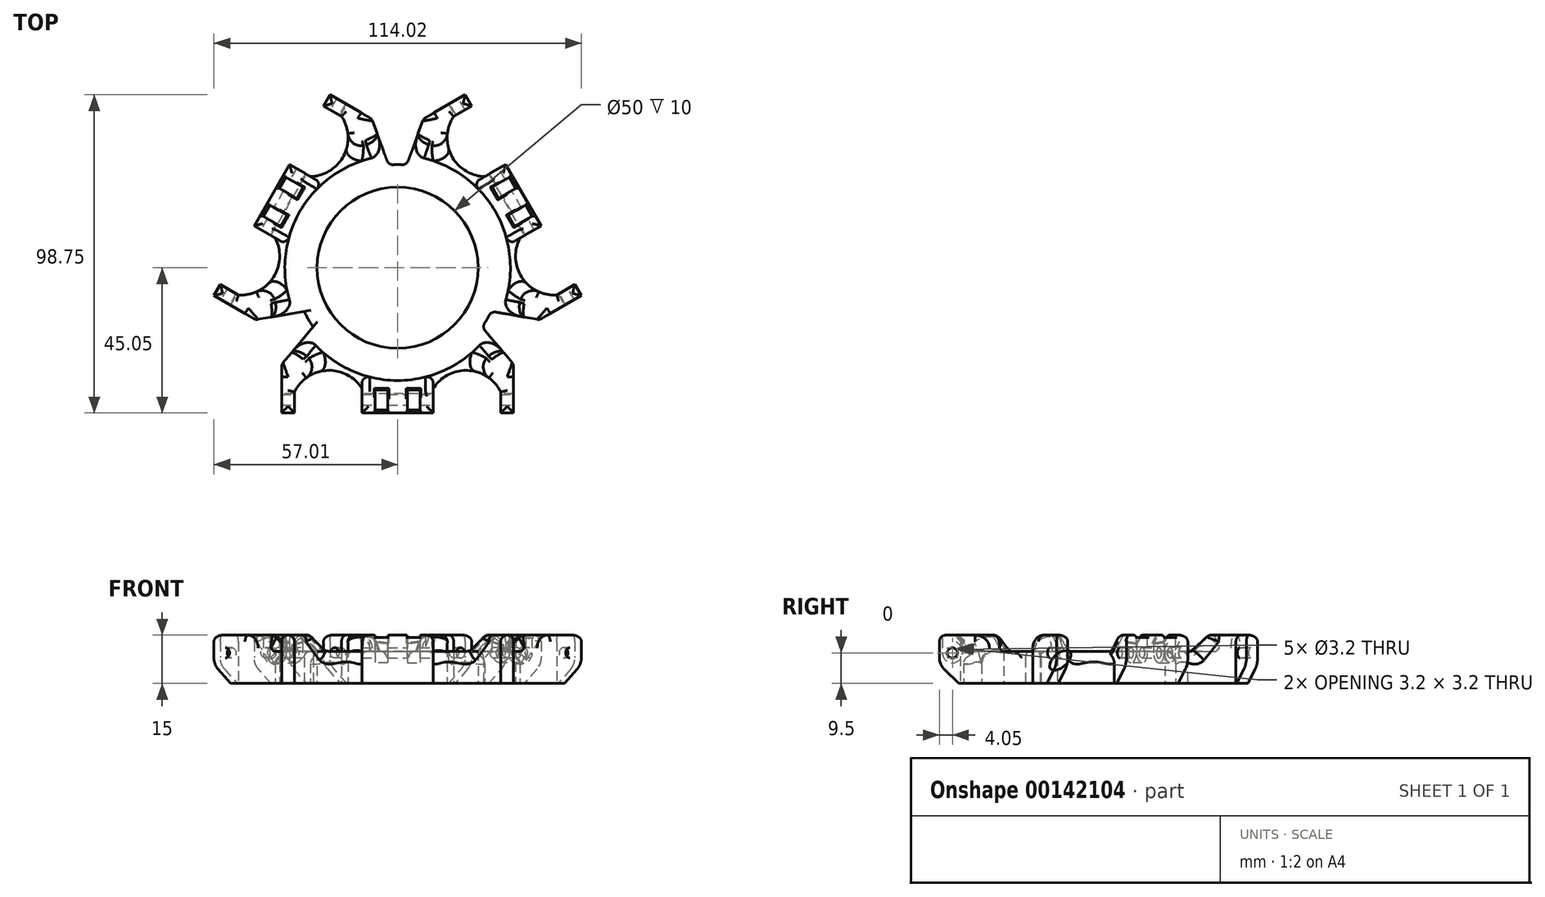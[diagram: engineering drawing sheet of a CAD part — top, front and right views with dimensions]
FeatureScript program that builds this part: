
annotation { "Feature Type Name" : "Feature", "Feature Type Description" : "" }
export const myFeature = defineFeature(function(context is Context, id is Id, definition is map)
    precondition{}
    {
        {
            assignVariable(context, id + "F0", {"name" : "JointHeight", "anyValue" : 18});
        }
        {
            var Q0;
            Q0=qCreatedBy(makeId("Top.planeOp"),FACE);
            var sketch = newSketch(context, id + "F1", { "sketchPlane" : qUnion([Q0])});
            skCircle(sketch, "E0", {"center": v(0, 0) * mm, "radius": 25 * mm});
            skCircle(sketch, "E1", {"center": v(0, 0) * mm, "radius": 32 * mm});
            skSolve(sketch);
        }
        {
            var Q0;
            Q0=qCreatedBy(makeId("Top.planeOp"),FACE);
            var sketch = newSketch(context, id + "F2", { "sketchPlane" : qUnion([Q0])});
            skLineSegment(sketch, "E2", {"start": v(-21.5, 50) * mm, "end": v(-21.5, -50) * mm, "construction": true});
            skLineSegment(sketch, "E3", {"start": v(21.5, 50) * mm, "end": v(21.5, -50) * mm, "construction": true});
            skLineSegment(sketch, "E4", {"start": v(-11, -50) * mm, "end": v(-11, -30.05) * mm, "construction": true});
            skLineSegment(sketch, "E5", {"start": v(11, -50) * mm, "end": v(11, -30.05) * mm, "construction": true});
            skLineSegment(sketch, "E6", {"start": v(-32, -50) * mm, "end": v(-32, 0) * mm, "construction": true});
            skLineSegment(sketch, "E7", {"start": v(32, -50) * mm, "end": v(32, 0) * mm, "construction": true});
            skLineSegment(sketch, "E8", {"start": v(0, -41.5) * mm, "end": v(0, -32) * mm, "construction": true});
            skLineSegment(sketch, "E9", {"start": v(-11, -30.05) * mm, "end": v(-11, -45.05) * mm});
            skLineSegment(sketch, "E10", {"start": v(-11, -45.05) * mm, "end": v(11, -45.05) * mm});
            skLineSegment(sketch, "E11", {"start": v(11, -45.05) * mm, "end": v(11, -30.05) * mm});
            skLineSegment(sketch, "E12", {"start": v(-32, -45.05) * mm, "end": v(-36, -45.05) * mm});
            skArc(sketch, "E13", {"start": v(-11, -30.05) * mm, "mid": v(0, -32) * mm, "end": v(11, -30.05) * mm});
            skLineSegment(sketch, "E14", {"start": v(-36, -45.05) * mm, "end": v(-36, -30.05) * mm});
            skLineSegment(sketch, "E15", {"start": v(-36, -30.05) * mm, "end": v(-26.2, -18.37) * mm});
            skCircle(sketch, "E16", {"center": v(-21.5, -41.5) * mm, "radius": 9.25 * mm, "construction": true});
            skLineSegment(sketch, "E17", {"start": v(-32, -45.05) * mm, "end": v(-32, -38.55) * mm});
            skArc(sketch, "E18", {"start": v(-11, -37.55) * mm, "mid": v(-21.8, -31.88) * mm, "end": v(-32, -38.55) * mm});
            skArc(sketch, "E19", {"start": v(-26.2, -18.37) * mm, "mid": v(-19.5, -25.38) * mm, "end": v(-11, -30.05) * mm});
            skLineSegment(sketch, "E20.MirrorCS", {"start": v(36, -45.05) * mm, "end": v(36, -30.05) * mm});
            skLineSegment(sketch, "E21.MirrorCS", {"start": v(32, -45.05) * mm, "end": v(36, -45.05) * mm});
            skLineSegment(sketch, "E22.MirrorCS", {"start": v(36, -30.05) * mm, "end": v(26.2, -18.37) * mm});
            skLineSegment(sketch, "E23.MirrorCS", {"start": v(32, -45.05) * mm, "end": v(32, -38.55) * mm});
            skArc(sketch, "E24.MirrorCS", {"start": v(11, -37.55) * mm, "mid": v(21.8, -31.88) * mm, "end": v(32, -38.55) * mm});
            skArc(sketch, "E25.MirrorCS", {"start": v(26.2, -18.37) * mm, "mid": v(19.5, -25.38) * mm, "end": v(11, -30.05) * mm});
            skSolve(sketch);
        }
        {
            var Q0;
            Q0=makeQuery(id+"F1.imprint","IMPRINT",FACE,{"disambiguationData":[TD([[makeQuery(id+"F1.imprint","IMPRINT",EDGE,{"derivedFrom":sQuery(id+"F1.wireOp",EDGE,"E0")}),-1.0]])]});
            extrude(context, id + "F3", {"entities" : qUnion([Q0]), "depth" : 10 * mm});
        }
        {
            var Q0;
            Q0=qSketchRegion(id+"F2",true);
            extrude(context, id + "F4", {"entities" : qUnion([Q0]), "depth" : (getVariable(context, 'JointHeight') - 3) * mm});
        }
        {
            var Q0;
            Q0=makeQuery(id+"F4.opExtrude","SWEPT_FACE",FACE,{"disambiguationData":[OSD([sQuery(id+"F2.wireOp",EDGE,"E20.MirrorCS")])]});
            var sketch = newSketch(context, id + "F5", { "sketchPlane" : qUnion([Q0])});
            skCircle(sketch, "E26", {"center": v(-41, 9.5) * mm, "radius": 1.6 * mm});
            skSolve(sketch);
        }
        {
            var Q0;
            Q0=makeQuery(id+"F5.imprint","IMPRINT",FACE,{"disambiguationData":[TD([[makeQuery(id+"F5.imprint","IMPRINT",EDGE,{"derivedFrom":sQuery(id+"F5.wireOp",EDGE,"E26")}),1.0]])]});
            var Q1;
            Q1=makeQuery(id+"F4.opExtrude","SWEPT_FACE",FACE,{"disambiguationData":[OSD([sQuery(id+"F2.wireOp",EDGE,"E14")])]});
            extrude(context, id + "F6", {"entities" : qUnion([Q0]), "operationType" : NewBodyOperationType.REMOVE, "endBound" : BoundingType.UP_TO_SURFACE, "oppositeDirection" : true, "endBoundEntityFace" : qUnion([Q1]), "depth" : 25 * mm});
        }
        {
            var Q0;
            Q0=makeQuery(id+"F4.opExtrude","SWEPT_BODY",BODY,{"disambiguationData":[OSD([sQuery(id+"F2.wireOp",EDGE,"E9"),sQuery(id+"F2.wireOp",EDGE,"E10"),sQuery(id+"F2.wireOp",EDGE,"E11"),sQuery(id+"F2.wireOp",EDGE,"E12"),sQuery(id+"F2.wireOp",EDGE,"E13"),sQuery(id+"F2.wireOp",EDGE,"E14"),sQuery(id+"F2.wireOp",EDGE,"E15"),sQuery(id+"F2.wireOp",EDGE,"E17"),sQuery(id+"F2.wireOp",EDGE,"E18"),sQuery(id+"F2.wireOp",EDGE,"E19"),sQuery(id+"F2.wireOp",EDGE,"E20.MirrorCS"),sQuery(id+"F2.wireOp",EDGE,"E21.MirrorCS"),sQuery(id+"F2.wireOp",EDGE,"E22.MirrorCS"),sQuery(id+"F2.wireOp",EDGE,"E23.MirrorCS"),sQuery(id+"F2.wireOp",EDGE,"E24.MirrorCS"),sQuery(id+"F2.wireOp",EDGE,"E25.MirrorCS")])]});
            var Q1;
            Q1=makeQuery(id+"F3.opExtrude","SWEPT_FACE",FACE,{"disambiguationData":[OSD([sQuery(id+"F1.wireOp",EDGE,"E1")])]});
            circularPattern(context, id + "F7", {"operationType" : NewBodyOperationType.ADD, "entities" : qUnion([Q0]), "axis" : qUnion([Q1]), "angle" : 120 * degree, "instanceCount" : 3});
        }
        {
            var Q0;
            Q0=makeQuery(id+"F4.opExtrude","CAP_EDGE",EDGE,{"disambiguationData":[OSD([sQuery(id+"F2.wireOp",EDGE,"E13"),sQuery(id+"F2.wireOp",EDGE,"E19"),sQuery(id+"F2.wireOp",EDGE,"E25.MirrorCS")])],"isStart":false});
            var Q1;
            Q1=makeQuery(id+"F7.opPattern","COPY",EDGE,{"derivedFrom":makeQuery(id+"F4.opExtrude","CAP_EDGE",EDGE,{"disambiguationData":[OSD([sQuery(id+"F2.wireOp",EDGE,"E13"),sQuery(id+"F2.wireOp",EDGE,"E19"),sQuery(id+"F2.wireOp",EDGE,"E25.MirrorCS")])],"isStart":false}),"instanceName":"1"});
            var Q2;
            Q2=makeQuery(id+"F7.opPattern","COPY",EDGE,{"derivedFrom":makeQuery(id+"F4.opExtrude","CAP_EDGE",EDGE,{"disambiguationData":[OSD([sQuery(id+"F2.wireOp",EDGE,"E13"),sQuery(id+"F2.wireOp",EDGE,"E19"),sQuery(id+"F2.wireOp",EDGE,"E25.MirrorCS")])],"isStart":false}),"instanceName":"2"});
            chamfer(context, id + "F8", {"entities" : qUnion([Q0, Q1, Q2]), "width" : 8 * mm});
        }
        {
            var Q0;
            Q0=makeQuery(id+"F8.opChamfer","BLEND_EDGE",EDGE,{"blendedFrom":[makeQuery(id+"F4.opExtrude","CAP_EDGE",EDGE,{"disambiguationData":[OSD([sQuery(id+"F2.wireOp",EDGE,"E13"),sQuery(id+"F2.wireOp",EDGE,"E19"),sQuery(id+"F2.wireOp",EDGE,"E25.MirrorCS")])],"isStart":false}),makeQuery(id+"F4.opExtrude","SWEPT_FACE",FACE,{"disambiguationData":[OSD([sQuery(id+"F2.wireOp",EDGE,"E24.MirrorCS")])]})],"blendedInto":[makeQuery(id+"F4.opExtrude","SWEPT_FACE",FACE,{"disambiguationData":[OSD([sQuery(id+"F2.wireOp",EDGE,"E24.MirrorCS")])]})]});
            var Q1;
            Q1=makeQuery(id+"F8.opChamfer","BLEND_EDGE",EDGE,{"blendedFrom":[makeQuery(id+"F4.opExtrude","CAP_EDGE",EDGE,{"disambiguationData":[OSD([sQuery(id+"F2.wireOp",EDGE,"E13"),sQuery(id+"F2.wireOp",EDGE,"E19"),sQuery(id+"F2.wireOp",EDGE,"E25.MirrorCS")])],"isStart":false}),makeQuery(id+"F4.opExtrude","SWEPT_FACE",FACE,{"disambiguationData":[OSD([sQuery(id+"F2.wireOp",EDGE,"E18")])]})],"blendedInto":[makeQuery(id+"F4.opExtrude","SWEPT_FACE",FACE,{"disambiguationData":[OSD([sQuery(id+"F2.wireOp",EDGE,"E18")])]})]});
            var Q2;
            Q2=makeQuery(id+"F8.opChamfer","BLEND_EDGE",EDGE,{"blendedFrom":[makeQuery(id+"F4.opExtrude","CAP_EDGE",EDGE,{"disambiguationData":[OSD([sQuery(id+"F2.wireOp",EDGE,"E13"),sQuery(id+"F2.wireOp",EDGE,"E19"),sQuery(id+"F2.wireOp",EDGE,"E25.MirrorCS")])],"isStart":false}),makeQuery(id+"F4.opExtrude","SWEPT_FACE",FACE,{"disambiguationData":[OSD([sQuery(id+"F2.wireOp",EDGE,"E22.MirrorCS")])]})],"blendedInto":[makeQuery(id+"F4.opExtrude","SWEPT_FACE",FACE,{"disambiguationData":[OSD([sQuery(id+"F2.wireOp",EDGE,"E22.MirrorCS")])]})]});
            var Q3;
            Q3=makeQuery(id+"F8.opChamfer","BLEND_EDGE",EDGE,{"blendedFrom":[makeQuery(id+"F4.opExtrude","CAP_EDGE",EDGE,{"disambiguationData":[OSD([sQuery(id+"F2.wireOp",EDGE,"E13"),sQuery(id+"F2.wireOp",EDGE,"E19"),sQuery(id+"F2.wireOp",EDGE,"E25.MirrorCS")])],"isStart":false}),makeQuery(id+"F4.opExtrude","SWEPT_FACE",FACE,{"disambiguationData":[OSD([sQuery(id+"F2.wireOp",EDGE,"E15")])]})],"blendedInto":[makeQuery(id+"F4.opExtrude","SWEPT_FACE",FACE,{"disambiguationData":[OSD([sQuery(id+"F2.wireOp",EDGE,"E15")])]})]});
            var Q4;
            Q4=makeQuery(id+"F8.opChamfer","BLEND_EDGE",EDGE,{"blendedFrom":[makeQuery(id+"F7.opPattern","COPY",EDGE,{"derivedFrom":makeQuery(id+"F4.opExtrude","CAP_EDGE",EDGE,{"disambiguationData":[OSD([sQuery(id+"F2.wireOp",EDGE,"E13"),sQuery(id+"F2.wireOp",EDGE,"E19"),sQuery(id+"F2.wireOp",EDGE,"E25.MirrorCS")])],"isStart":false}),"instanceName":"2"}),makeQuery(id+"F7.opPattern","COPY",FACE,{"derivedFrom":makeQuery(id+"F4.opExtrude","SWEPT_FACE",FACE,{"disambiguationData":[OSD([sQuery(id+"F2.wireOp",EDGE,"E18")])]}),"instanceName":"2"})],"blendedInto":[makeQuery(id+"F7.opPattern","COPY",FACE,{"derivedFrom":makeQuery(id+"F4.opExtrude","SWEPT_FACE",FACE,{"disambiguationData":[OSD([sQuery(id+"F2.wireOp",EDGE,"E18")])]}),"instanceName":"2"})]});
            var Q5;
            Q5=makeQuery(id+"F8.opChamfer","BLEND_EDGE",EDGE,{"blendedFrom":[makeQuery(id+"F7.opPattern","COPY",EDGE,{"derivedFrom":makeQuery(id+"F4.opExtrude","CAP_EDGE",EDGE,{"disambiguationData":[OSD([sQuery(id+"F2.wireOp",EDGE,"E13"),sQuery(id+"F2.wireOp",EDGE,"E19"),sQuery(id+"F2.wireOp",EDGE,"E25.MirrorCS")])],"isStart":false}),"instanceName":"1"}),makeQuery(id+"F7.opPattern","COPY",FACE,{"derivedFrom":makeQuery(id+"F4.opExtrude","SWEPT_FACE",FACE,{"disambiguationData":[OSD([sQuery(id+"F2.wireOp",EDGE,"E24.MirrorCS")])]}),"instanceName":"1"})],"blendedInto":[makeQuery(id+"F7.opPattern","COPY",FACE,{"derivedFrom":makeQuery(id+"F4.opExtrude","SWEPT_FACE",FACE,{"disambiguationData":[OSD([sQuery(id+"F2.wireOp",EDGE,"E24.MirrorCS")])]}),"instanceName":"1"})]});
            var Q6;
            Q6=makeQuery(id+"F8.opChamfer","BLEND_EDGE",EDGE,{"blendedFrom":[makeQuery(id+"F7.opPattern","COPY",EDGE,{"derivedFrom":makeQuery(id+"F4.opExtrude","CAP_EDGE",EDGE,{"disambiguationData":[OSD([sQuery(id+"F2.wireOp",EDGE,"E13"),sQuery(id+"F2.wireOp",EDGE,"E19"),sQuery(id+"F2.wireOp",EDGE,"E25.MirrorCS")])],"isStart":false}),"instanceName":"1"}),makeQuery(id+"F7.opPattern","COPY",FACE,{"derivedFrom":makeQuery(id+"F4.opExtrude","SWEPT_FACE",FACE,{"disambiguationData":[OSD([sQuery(id+"F2.wireOp",EDGE,"E18")])]}),"instanceName":"1"})],"blendedInto":[makeQuery(id+"F7.opPattern","COPY",FACE,{"derivedFrom":makeQuery(id+"F4.opExtrude","SWEPT_FACE",FACE,{"disambiguationData":[OSD([sQuery(id+"F2.wireOp",EDGE,"E18")])]}),"instanceName":"1"})]});
            var Q7;
            Q7=makeQuery(id+"F8.opChamfer","BLEND_EDGE",EDGE,{"blendedFrom":[makeQuery(id+"F7.opPattern","COPY",EDGE,{"derivedFrom":makeQuery(id+"F4.opExtrude","CAP_EDGE",EDGE,{"disambiguationData":[OSD([sQuery(id+"F2.wireOp",EDGE,"E13"),sQuery(id+"F2.wireOp",EDGE,"E19"),sQuery(id+"F2.wireOp",EDGE,"E25.MirrorCS")])],"isStart":false}),"instanceName":"2"}),makeQuery(id+"F7.opPattern","COPY",FACE,{"derivedFrom":makeQuery(id+"F4.opExtrude","SWEPT_FACE",FACE,{"disambiguationData":[OSD([sQuery(id+"F2.wireOp",EDGE,"E24.MirrorCS")])]}),"instanceName":"2"})],"blendedInto":[makeQuery(id+"F7.opPattern","COPY",FACE,{"derivedFrom":makeQuery(id+"F4.opExtrude","SWEPT_FACE",FACE,{"disambiguationData":[OSD([sQuery(id+"F2.wireOp",EDGE,"E24.MirrorCS")])]}),"instanceName":"2"})]});
            var Q8;
            Q8=makeQuery(id+"F8.opChamfer","BLEND_EDGE",EDGE,{"blendedFrom":[makeQuery(id+"F7.opPattern","COPY",EDGE,{"derivedFrom":makeQuery(id+"F4.opExtrude","CAP_EDGE",EDGE,{"disambiguationData":[OSD([sQuery(id+"F2.wireOp",EDGE,"E13"),sQuery(id+"F2.wireOp",EDGE,"E19"),sQuery(id+"F2.wireOp",EDGE,"E25.MirrorCS")])],"isStart":false}),"instanceName":"1"}),makeQuery(id+"F7.opPattern","COPY",FACE,{"derivedFrom":makeQuery(id+"F4.opExtrude","SWEPT_FACE",FACE,{"disambiguationData":[OSD([sQuery(id+"F2.wireOp",EDGE,"E22.MirrorCS")])]}),"instanceName":"1"})],"blendedInto":[makeQuery(id+"F7.opPattern","COPY",FACE,{"derivedFrom":makeQuery(id+"F4.opExtrude","SWEPT_FACE",FACE,{"disambiguationData":[OSD([sQuery(id+"F2.wireOp",EDGE,"E22.MirrorCS")])]}),"instanceName":"1"})]});
            var Q9;
            Q9=makeQuery(id+"F8.opChamfer","BLEND_EDGE",EDGE,{"blendedFrom":[makeQuery(id+"F7.opPattern","COPY",EDGE,{"derivedFrom":makeQuery(id+"F4.opExtrude","CAP_EDGE",EDGE,{"disambiguationData":[OSD([sQuery(id+"F2.wireOp",EDGE,"E13"),sQuery(id+"F2.wireOp",EDGE,"E19"),sQuery(id+"F2.wireOp",EDGE,"E25.MirrorCS")])],"isStart":false}),"instanceName":"1"}),makeQuery(id+"F7.opPattern","COPY",FACE,{"derivedFrom":makeQuery(id+"F4.opExtrude","SWEPT_FACE",FACE,{"disambiguationData":[OSD([sQuery(id+"F2.wireOp",EDGE,"E15")])]}),"instanceName":"1"})],"blendedInto":[makeQuery(id+"F7.opPattern","COPY",FACE,{"derivedFrom":makeQuery(id+"F4.opExtrude","SWEPT_FACE",FACE,{"disambiguationData":[OSD([sQuery(id+"F2.wireOp",EDGE,"E15")])]}),"instanceName":"1"})]});
            var Q10;
            Q10=makeQuery(id+"F8.opChamfer","BLEND_EDGE",EDGE,{"blendedFrom":[makeQuery(id+"F7.opPattern","COPY",EDGE,{"derivedFrom":makeQuery(id+"F4.opExtrude","CAP_EDGE",EDGE,{"disambiguationData":[OSD([sQuery(id+"F2.wireOp",EDGE,"E13"),sQuery(id+"F2.wireOp",EDGE,"E19"),sQuery(id+"F2.wireOp",EDGE,"E25.MirrorCS")])],"isStart":false}),"instanceName":"2"}),makeQuery(id+"F7.opPattern","COPY",FACE,{"derivedFrom":makeQuery(id+"F4.opExtrude","SWEPT_FACE",FACE,{"disambiguationData":[OSD([sQuery(id+"F2.wireOp",EDGE,"E22.MirrorCS")])]}),"instanceName":"2"})],"blendedInto":[makeQuery(id+"F7.opPattern","COPY",FACE,{"derivedFrom":makeQuery(id+"F4.opExtrude","SWEPT_FACE",FACE,{"disambiguationData":[OSD([sQuery(id+"F2.wireOp",EDGE,"E22.MirrorCS")])]}),"instanceName":"2"})]});
            var Q11;
            Q11=makeQuery(id+"F7.opPattern","COPY",EDGE,{"derivedFrom":makeQuery(id+"F4.opExtrude","CAP_EDGE",EDGE,{"disambiguationData":[OSD([sQuery(id+"F2.wireOp",EDGE,"E15")])],"isStart":false}),"instanceName":"2"});
            var Q12;
            Q12=makeQuery(id+"F4.opExtrude","CAP_EDGE",EDGE,{"disambiguationData":[OSD([sQuery(id+"F2.wireOp",EDGE,"E22.MirrorCS")])],"isStart":false});
            var Q13;
            Q13=makeQuery(id+"F8.opChamfer","BLEND_EDGE",EDGE,{"blendedFrom":[makeQuery(id+"F7.opPattern","COPY",EDGE,{"derivedFrom":makeQuery(id+"F4.opExtrude","CAP_EDGE",EDGE,{"disambiguationData":[OSD([sQuery(id+"F2.wireOp",EDGE,"E13"),sQuery(id+"F2.wireOp",EDGE,"E19"),sQuery(id+"F2.wireOp",EDGE,"E25.MirrorCS")])],"isStart":false}),"instanceName":"2"}),makeQuery(id+"F7.opPattern","COPY",FACE,{"derivedFrom":makeQuery(id+"F4.opExtrude","SWEPT_FACE",FACE,{"disambiguationData":[OSD([sQuery(id+"F2.wireOp",EDGE,"E15")])]}),"instanceName":"2"})],"blendedInto":[makeQuery(id+"F7.opPattern","COPY",FACE,{"derivedFrom":makeQuery(id+"F4.opExtrude","SWEPT_FACE",FACE,{"disambiguationData":[OSD([sQuery(id+"F2.wireOp",EDGE,"E15")])]}),"instanceName":"2"})]});
            var Q14;
            {var subQ0=sQuery(id+"F1.wireOp",EDGE,"E1");Q14=makeQuery(id+"F8.opChamfer","TWEAK_EDGE",EDGE,{"derivedFrom":[makeQuery(id+"F7.boolean.opBoolean","TWEAK_VERTEX",VERTEX,{"derivedFrom":[makeQuery(id+"F3.opExtrude","CAP_FACE",FACE,{"disambiguationData":[OSD([sQuery(id+"F1.wireOp",EDGE,"E0"),subQ0])],"isStart":false}),makeQuery(id+"F3.opExtrude","SWEPT_FACE",FACE,{"disambiguationData":[OSD([subQ0])]}),makeQuery(id+"F7.opPattern","COPY",FACE,{"derivedFrom":makeQuery(id+"F4.opExtrude","SWEPT_FACE",FACE,{"disambiguationData":[OSD([sQuery(id+"F2.wireOp",EDGE,"E13"),sQuery(id+"F2.wireOp",EDGE,"E19"),sQuery(id+"F2.wireOp",EDGE,"E25.MirrorCS")])]}),"instanceName":"2"}),makeQuery(id+"F7.opPattern","COPY",FACE,{"derivedFrom":makeQuery(id+"F4.opExtrude","SWEPT_FACE",FACE,{"disambiguationData":[OSD([sQuery(id+"F2.wireOp",EDGE,"E22.MirrorCS")])]}),"instanceName":"2"})]})]});}
            var Q15;
            {var subQ0=sQuery(id+"F1.wireOp",EDGE,"E1");Q15=makeQuery(id+"F8.opChamfer","TWEAK_EDGE",EDGE,{"derivedFrom":[makeQuery(id+"F7.boolean.opBoolean","TWEAK_VERTEX",VERTEX,{"derivedFrom":[makeQuery(id+"F3.opExtrude","CAP_FACE",FACE,{"disambiguationData":[OSD([sQuery(id+"F1.wireOp",EDGE,"E0"),subQ0])],"isStart":false}),makeQuery(id+"F3.opExtrude","SWEPT_FACE",FACE,{"disambiguationData":[OSD([subQ0])]}),makeQuery(id+"F7.opPattern","COPY",FACE,{"derivedFrom":makeQuery(id+"F4.opExtrude","SWEPT_FACE",FACE,{"disambiguationData":[OSD([sQuery(id+"F2.wireOp",EDGE,"E13"),sQuery(id+"F2.wireOp",EDGE,"E19"),sQuery(id+"F2.wireOp",EDGE,"E25.MirrorCS")])]}),"instanceName":"1"}),makeQuery(id+"F7.opPattern","COPY",FACE,{"derivedFrom":makeQuery(id+"F4.opExtrude","SWEPT_FACE",FACE,{"disambiguationData":[OSD([sQuery(id+"F2.wireOp",EDGE,"E15")])]}),"instanceName":"1"})]})]});}
            var Q16;
            {var subQ0=sQuery(id+"F1.wireOp",EDGE,"E1");Q16=makeQuery(id+"F8.opChamfer","TWEAK_EDGE",EDGE,{"derivedFrom":[makeQuery(id+"F7.boolean.opBoolean","TWEAK_VERTEX",VERTEX,{"derivedFrom":[makeQuery(id+"F3.opExtrude","CAP_FACE",FACE,{"disambiguationData":[OSD([sQuery(id+"F1.wireOp",EDGE,"E0"),subQ0])],"isStart":false}),makeQuery(id+"F3.opExtrude","SWEPT_FACE",FACE,{"disambiguationData":[OSD([subQ0])]}),makeQuery(id+"F7.opPattern","COPY",FACE,{"derivedFrom":makeQuery(id+"F4.opExtrude","SWEPT_FACE",FACE,{"disambiguationData":[OSD([sQuery(id+"F2.wireOp",EDGE,"E13"),sQuery(id+"F2.wireOp",EDGE,"E19"),sQuery(id+"F2.wireOp",EDGE,"E25.MirrorCS")])]}),"instanceName":"1"}),makeQuery(id+"F7.opPattern","COPY",FACE,{"derivedFrom":makeQuery(id+"F4.opExtrude","SWEPT_FACE",FACE,{"disambiguationData":[OSD([sQuery(id+"F2.wireOp",EDGE,"E22.MirrorCS")])]}),"instanceName":"1"})]})]});}
            var Q17;
            {var subQ0=sQuery(id+"F1.wireOp",EDGE,"E1");Q17=makeQuery(id+"F8.opChamfer","TWEAK_EDGE",EDGE,{"derivedFrom":[makeQuery(id+"F7.boolean.opBoolean","TWEAK_VERTEX",VERTEX,{"derivedFrom":[makeQuery(id+"F3.opExtrude","CAP_FACE",FACE,{"disambiguationData":[OSD([sQuery(id+"F1.wireOp",EDGE,"E0"),subQ0])],"isStart":false}),makeQuery(id+"F3.opExtrude","SWEPT_FACE",FACE,{"disambiguationData":[OSD([subQ0])]}),makeQuery(id+"F4.opExtrude","SWEPT_FACE",FACE,{"disambiguationData":[OSD([sQuery(id+"F2.wireOp",EDGE,"E13"),sQuery(id+"F2.wireOp",EDGE,"E19"),sQuery(id+"F2.wireOp",EDGE,"E25.MirrorCS")])]}),makeQuery(id+"F4.opExtrude","SWEPT_FACE",FACE,{"disambiguationData":[OSD([sQuery(id+"F2.wireOp",EDGE,"E15")])]})]})]});}
            var Q18;
            Q18=makeQuery(id+"F4.opExtrude","CAP_EDGE",EDGE,{"disambiguationData":[OSD([sQuery(id+"F2.wireOp",EDGE,"E15")])],"isStart":false});
            var Q19;
            Q19=makeQuery(id+"F7.opPattern","COPY",EDGE,{"derivedFrom":makeQuery(id+"F4.opExtrude","CAP_EDGE",EDGE,{"disambiguationData":[OSD([sQuery(id+"F2.wireOp",EDGE,"E22.MirrorCS")])],"isStart":false}),"instanceName":"1"});
            var Q20;
            Q20=makeQuery(id+"F7.opPattern","COPY",EDGE,{"derivedFrom":makeQuery(id+"F4.opExtrude","CAP_EDGE",EDGE,{"disambiguationData":[OSD([sQuery(id+"F2.wireOp",EDGE,"E22.MirrorCS")])],"isStart":false}),"instanceName":"2"});
            var Q21;
            Q21=makeQuery(id+"F7.opPattern","COPY",EDGE,{"derivedFrom":makeQuery(id+"F4.opExtrude","CAP_EDGE",EDGE,{"disambiguationData":[OSD([sQuery(id+"F2.wireOp",EDGE,"E15")])],"isStart":false}),"instanceName":"1"});
            var Q22;
            {var subQ0=sQuery(id+"F1.wireOp",EDGE,"E1");Q22=makeQuery(id+"F8.opChamfer","TWEAK_EDGE",EDGE,{"derivedFrom":[makeQuery(id+"F7.boolean.opBoolean","TWEAK_VERTEX",VERTEX,{"derivedFrom":[makeQuery(id+"F3.opExtrude","CAP_FACE",FACE,{"disambiguationData":[OSD([sQuery(id+"F1.wireOp",EDGE,"E0"),subQ0])],"isStart":false}),makeQuery(id+"F3.opExtrude","SWEPT_FACE",FACE,{"disambiguationData":[OSD([subQ0])]}),makeQuery(id+"F7.opPattern","COPY",FACE,{"derivedFrom":makeQuery(id+"F4.opExtrude","SWEPT_FACE",FACE,{"disambiguationData":[OSD([sQuery(id+"F2.wireOp",EDGE,"E13"),sQuery(id+"F2.wireOp",EDGE,"E19"),sQuery(id+"F2.wireOp",EDGE,"E25.MirrorCS")])]}),"instanceName":"2"}),makeQuery(id+"F7.opPattern","COPY",FACE,{"derivedFrom":makeQuery(id+"F4.opExtrude","SWEPT_FACE",FACE,{"disambiguationData":[OSD([sQuery(id+"F2.wireOp",EDGE,"E15")])]}),"instanceName":"2"})]})]});}
            var Q23;
            {var subQ0=sQuery(id+"F1.wireOp",EDGE,"E1");Q23=makeQuery(id+"F8.opChamfer","TWEAK_EDGE",EDGE,{"derivedFrom":[makeQuery(id+"F7.boolean.opBoolean","TWEAK_VERTEX",VERTEX,{"derivedFrom":[makeQuery(id+"F3.opExtrude","CAP_FACE",FACE,{"disambiguationData":[OSD([sQuery(id+"F1.wireOp",EDGE,"E0"),subQ0])],"isStart":false}),makeQuery(id+"F3.opExtrude","SWEPT_FACE",FACE,{"disambiguationData":[OSD([subQ0])]}),makeQuery(id+"F4.opExtrude","SWEPT_FACE",FACE,{"disambiguationData":[OSD([sQuery(id+"F2.wireOp",EDGE,"E13"),sQuery(id+"F2.wireOp",EDGE,"E19"),sQuery(id+"F2.wireOp",EDGE,"E25.MirrorCS")])]}),makeQuery(id+"F4.opExtrude","SWEPT_FACE",FACE,{"disambiguationData":[OSD([sQuery(id+"F2.wireOp",EDGE,"E22.MirrorCS")])]})]})]});}
            fillet(context, id + "F9", {"entities" : qUnion([Q0, Q1, Q2, Q3, Q4, Q5, Q6, Q7, Q8, Q9, Q10, Q11, Q12, Q13, Q14, Q15, Q16, Q17, Q18, Q19, Q20, Q21, Q22, Q23]), "radius" : 4 * mm, "tangentPropagation" : true, "allowEdgeOverflow" : false});
        }
        {
            var Q0;
            Q0=makeQuery(id+"F8.opChamfer","BLEND_EDGE",EDGE,{"blendedFrom":[makeQuery(id+"F7.opPattern","COPY",EDGE,{"derivedFrom":makeQuery(id+"F4.opExtrude","CAP_EDGE",EDGE,{"disambiguationData":[OSD([sQuery(id+"F2.wireOp",EDGE,"E13"),sQuery(id+"F2.wireOp",EDGE,"E19"),sQuery(id+"F2.wireOp",EDGE,"E25.MirrorCS")])],"isStart":false}),"instanceName":"1"}),makeQuery(id+"F7.opPattern","COPY",FACE,{"derivedFrom":makeQuery(id+"F4.opExtrude","SWEPT_FACE",FACE,{"disambiguationData":[OSD([sQuery(id+"F2.wireOp",EDGE,"E11")])]}),"instanceName":"1"})],"blendedInto":[makeQuery(id+"F7.opPattern","COPY",FACE,{"derivedFrom":makeQuery(id+"F4.opExtrude","SWEPT_FACE",FACE,{"disambiguationData":[OSD([sQuery(id+"F2.wireOp",EDGE,"E11")])]}),"instanceName":"1"})]});
            var Q1;
            Q1=makeQuery(id+"F8.opChamfer","BLEND_EDGE",EDGE,{"blendedFrom":[makeQuery(id+"F7.opPattern","COPY",EDGE,{"derivedFrom":makeQuery(id+"F4.opExtrude","CAP_EDGE",EDGE,{"disambiguationData":[OSD([sQuery(id+"F2.wireOp",EDGE,"E13"),sQuery(id+"F2.wireOp",EDGE,"E19"),sQuery(id+"F2.wireOp",EDGE,"E25.MirrorCS")])],"isStart":false}),"instanceName":"1"}),makeQuery(id+"F7.opPattern","COPY",FACE,{"derivedFrom":makeQuery(id+"F4.opExtrude","SWEPT_FACE",FACE,{"disambiguationData":[OSD([sQuery(id+"F2.wireOp",EDGE,"E9")])]}),"instanceName":"1"})],"blendedInto":[makeQuery(id+"F7.opPattern","COPY",FACE,{"derivedFrom":makeQuery(id+"F4.opExtrude","SWEPT_FACE",FACE,{"disambiguationData":[OSD([sQuery(id+"F2.wireOp",EDGE,"E9")])]}),"instanceName":"1"})]});
            var Q2;
            Q2=makeQuery(id+"F8.opChamfer","BLEND_EDGE",EDGE,{"blendedFrom":[makeQuery(id+"F7.opPattern","COPY",EDGE,{"derivedFrom":makeQuery(id+"F4.opExtrude","CAP_EDGE",EDGE,{"disambiguationData":[OSD([sQuery(id+"F2.wireOp",EDGE,"E13"),sQuery(id+"F2.wireOp",EDGE,"E19"),sQuery(id+"F2.wireOp",EDGE,"E25.MirrorCS")])],"isStart":false}),"instanceName":"2"}),makeQuery(id+"F7.opPattern","COPY",FACE,{"derivedFrom":makeQuery(id+"F4.opExtrude","SWEPT_FACE",FACE,{"disambiguationData":[OSD([sQuery(id+"F2.wireOp",EDGE,"E11")])]}),"instanceName":"2"})],"blendedInto":[makeQuery(id+"F7.opPattern","COPY",FACE,{"derivedFrom":makeQuery(id+"F4.opExtrude","SWEPT_FACE",FACE,{"disambiguationData":[OSD([sQuery(id+"F2.wireOp",EDGE,"E11")])]}),"instanceName":"2"})]});
            var Q3;
            Q3=makeQuery(id+"F8.opChamfer","BLEND_EDGE",EDGE,{"blendedFrom":[makeQuery(id+"F7.opPattern","COPY",EDGE,{"derivedFrom":makeQuery(id+"F4.opExtrude","CAP_EDGE",EDGE,{"disambiguationData":[OSD([sQuery(id+"F2.wireOp",EDGE,"E13"),sQuery(id+"F2.wireOp",EDGE,"E19"),sQuery(id+"F2.wireOp",EDGE,"E25.MirrorCS")])],"isStart":false}),"instanceName":"2"}),makeQuery(id+"F7.opPattern","COPY",FACE,{"derivedFrom":makeQuery(id+"F4.opExtrude","SWEPT_FACE",FACE,{"disambiguationData":[OSD([sQuery(id+"F2.wireOp",EDGE,"E9")])]}),"instanceName":"2"})],"blendedInto":[makeQuery(id+"F7.opPattern","COPY",FACE,{"derivedFrom":makeQuery(id+"F4.opExtrude","SWEPT_FACE",FACE,{"disambiguationData":[OSD([sQuery(id+"F2.wireOp",EDGE,"E9")])]}),"instanceName":"2"})]});
            var Q4;
            Q4=makeQuery(id+"F8.opChamfer","BLEND_EDGE",EDGE,{"blendedFrom":[makeQuery(id+"F4.opExtrude","CAP_EDGE",EDGE,{"disambiguationData":[OSD([sQuery(id+"F2.wireOp",EDGE,"E13"),sQuery(id+"F2.wireOp",EDGE,"E19"),sQuery(id+"F2.wireOp",EDGE,"E25.MirrorCS")])],"isStart":false}),makeQuery(id+"F4.opExtrude","SWEPT_FACE",FACE,{"disambiguationData":[OSD([sQuery(id+"F2.wireOp",EDGE,"E11")])]})],"blendedInto":[makeQuery(id+"F4.opExtrude","SWEPT_FACE",FACE,{"disambiguationData":[OSD([sQuery(id+"F2.wireOp",EDGE,"E11")])]})]});
            var Q5;
            Q5=makeQuery(id+"F8.opChamfer","BLEND_EDGE",EDGE,{"blendedFrom":[makeQuery(id+"F4.opExtrude","CAP_EDGE",EDGE,{"disambiguationData":[OSD([sQuery(id+"F2.wireOp",EDGE,"E13"),sQuery(id+"F2.wireOp",EDGE,"E19"),sQuery(id+"F2.wireOp",EDGE,"E25.MirrorCS")])],"isStart":false}),makeQuery(id+"F4.opExtrude","SWEPT_FACE",FACE,{"disambiguationData":[OSD([sQuery(id+"F2.wireOp",EDGE,"E9")])]})],"blendedInto":[makeQuery(id+"F4.opExtrude","SWEPT_FACE",FACE,{"disambiguationData":[OSD([sQuery(id+"F2.wireOp",EDGE,"E9")])]})]});
            var Q6;
            Q6=makeQuery(id+"F8.opChamfer","SPLIT",FACE,{"disambiguationData":[OD(0.0)],"derivedFrom":makeQuery(id+"F4.opExtrude","CAP_FACE",FACE,{"disambiguationData":[OSD([sQuery(id+"F2.wireOp",EDGE,"E9"),sQuery(id+"F2.wireOp",EDGE,"E10"),sQuery(id+"F2.wireOp",EDGE,"E11"),sQuery(id+"F2.wireOp",EDGE,"E12"),sQuery(id+"F2.wireOp",EDGE,"E13"),sQuery(id+"F2.wireOp",EDGE,"E14"),sQuery(id+"F2.wireOp",EDGE,"E15"),sQuery(id+"F2.wireOp",EDGE,"E17"),sQuery(id+"F2.wireOp",EDGE,"E18"),sQuery(id+"F2.wireOp",EDGE,"E19"),sQuery(id+"F2.wireOp",EDGE,"E20.MirrorCS"),sQuery(id+"F2.wireOp",EDGE,"E21.MirrorCS"),sQuery(id+"F2.wireOp",EDGE,"E22.MirrorCS"),sQuery(id+"F2.wireOp",EDGE,"E23.MirrorCS"),sQuery(id+"F2.wireOp",EDGE,"E24.MirrorCS"),sQuery(id+"F2.wireOp",EDGE,"E25.MirrorCS")])],"isStart":false})});
            var Q7;
            Q7=makeQuery(id+"F8.opChamfer","SPLIT",FACE,{"disambiguationData":[OD(1.0)],"derivedFrom":makeQuery(id+"F4.opExtrude","CAP_FACE",FACE,{"disambiguationData":[OSD([sQuery(id+"F2.wireOp",EDGE,"E9"),sQuery(id+"F2.wireOp",EDGE,"E10"),sQuery(id+"F2.wireOp",EDGE,"E11"),sQuery(id+"F2.wireOp",EDGE,"E12"),sQuery(id+"F2.wireOp",EDGE,"E13"),sQuery(id+"F2.wireOp",EDGE,"E14"),sQuery(id+"F2.wireOp",EDGE,"E15"),sQuery(id+"F2.wireOp",EDGE,"E17"),sQuery(id+"F2.wireOp",EDGE,"E18"),sQuery(id+"F2.wireOp",EDGE,"E19"),sQuery(id+"F2.wireOp",EDGE,"E20.MirrorCS"),sQuery(id+"F2.wireOp",EDGE,"E21.MirrorCS"),sQuery(id+"F2.wireOp",EDGE,"E22.MirrorCS"),sQuery(id+"F2.wireOp",EDGE,"E23.MirrorCS"),sQuery(id+"F2.wireOp",EDGE,"E24.MirrorCS"),sQuery(id+"F2.wireOp",EDGE,"E25.MirrorCS")])],"isStart":false})});
            var Q8;
            Q8=makeQuery(id+"F8.opChamfer","SPLIT",FACE,{"disambiguationData":[OD(2.0)],"derivedFrom":makeQuery(id+"F7.opPattern","COPY",FACE,{"derivedFrom":makeQuery(id+"F4.opExtrude","CAP_FACE",FACE,{"disambiguationData":[OSD([sQuery(id+"F2.wireOp",EDGE,"E9"),sQuery(id+"F2.wireOp",EDGE,"E10"),sQuery(id+"F2.wireOp",EDGE,"E11"),sQuery(id+"F2.wireOp",EDGE,"E12"),sQuery(id+"F2.wireOp",EDGE,"E13"),sQuery(id+"F2.wireOp",EDGE,"E14"),sQuery(id+"F2.wireOp",EDGE,"E15"),sQuery(id+"F2.wireOp",EDGE,"E17"),sQuery(id+"F2.wireOp",EDGE,"E18"),sQuery(id+"F2.wireOp",EDGE,"E19"),sQuery(id+"F2.wireOp",EDGE,"E20.MirrorCS"),sQuery(id+"F2.wireOp",EDGE,"E21.MirrorCS"),sQuery(id+"F2.wireOp",EDGE,"E22.MirrorCS"),sQuery(id+"F2.wireOp",EDGE,"E23.MirrorCS"),sQuery(id+"F2.wireOp",EDGE,"E24.MirrorCS"),sQuery(id+"F2.wireOp",EDGE,"E25.MirrorCS")])],"isStart":false}),"instanceName":"1"})});
            var Q9;
            Q9=makeQuery(id+"F8.opChamfer","SPLIT",FACE,{"disambiguationData":[OD(1.0)],"derivedFrom":makeQuery(id+"F7.opPattern","COPY",FACE,{"derivedFrom":makeQuery(id+"F4.opExtrude","CAP_FACE",FACE,{"disambiguationData":[OSD([sQuery(id+"F2.wireOp",EDGE,"E9"),sQuery(id+"F2.wireOp",EDGE,"E10"),sQuery(id+"F2.wireOp",EDGE,"E11"),sQuery(id+"F2.wireOp",EDGE,"E12"),sQuery(id+"F2.wireOp",EDGE,"E13"),sQuery(id+"F2.wireOp",EDGE,"E14"),sQuery(id+"F2.wireOp",EDGE,"E15"),sQuery(id+"F2.wireOp",EDGE,"E17"),sQuery(id+"F2.wireOp",EDGE,"E18"),sQuery(id+"F2.wireOp",EDGE,"E19"),sQuery(id+"F2.wireOp",EDGE,"E20.MirrorCS"),sQuery(id+"F2.wireOp",EDGE,"E21.MirrorCS"),sQuery(id+"F2.wireOp",EDGE,"E22.MirrorCS"),sQuery(id+"F2.wireOp",EDGE,"E23.MirrorCS"),sQuery(id+"F2.wireOp",EDGE,"E24.MirrorCS"),sQuery(id+"F2.wireOp",EDGE,"E25.MirrorCS")])],"isStart":false}),"instanceName":"1"})});
            var Q10;
            Q10=makeQuery(id+"F8.opChamfer","SPLIT",FACE,{"disambiguationData":[OD(0.0)],"derivedFrom":makeQuery(id+"F7.opPattern","COPY",FACE,{"derivedFrom":makeQuery(id+"F4.opExtrude","CAP_FACE",FACE,{"disambiguationData":[OSD([sQuery(id+"F2.wireOp",EDGE,"E9"),sQuery(id+"F2.wireOp",EDGE,"E10"),sQuery(id+"F2.wireOp",EDGE,"E11"),sQuery(id+"F2.wireOp",EDGE,"E12"),sQuery(id+"F2.wireOp",EDGE,"E13"),sQuery(id+"F2.wireOp",EDGE,"E14"),sQuery(id+"F2.wireOp",EDGE,"E15"),sQuery(id+"F2.wireOp",EDGE,"E17"),sQuery(id+"F2.wireOp",EDGE,"E18"),sQuery(id+"F2.wireOp",EDGE,"E19"),sQuery(id+"F2.wireOp",EDGE,"E20.MirrorCS"),sQuery(id+"F2.wireOp",EDGE,"E21.MirrorCS"),sQuery(id+"F2.wireOp",EDGE,"E22.MirrorCS"),sQuery(id+"F2.wireOp",EDGE,"E23.MirrorCS"),sQuery(id+"F2.wireOp",EDGE,"E24.MirrorCS"),sQuery(id+"F2.wireOp",EDGE,"E25.MirrorCS")])],"isStart":false}),"instanceName":"1"})});
            var Q11;
            Q11=makeQuery(id+"F8.opChamfer","SPLIT",FACE,{"disambiguationData":[OD(2.0)],"derivedFrom":makeQuery(id+"F7.opPattern","COPY",FACE,{"derivedFrom":makeQuery(id+"F4.opExtrude","CAP_FACE",FACE,{"disambiguationData":[OSD([sQuery(id+"F2.wireOp",EDGE,"E9"),sQuery(id+"F2.wireOp",EDGE,"E10"),sQuery(id+"F2.wireOp",EDGE,"E11"),sQuery(id+"F2.wireOp",EDGE,"E12"),sQuery(id+"F2.wireOp",EDGE,"E13"),sQuery(id+"F2.wireOp",EDGE,"E14"),sQuery(id+"F2.wireOp",EDGE,"E15"),sQuery(id+"F2.wireOp",EDGE,"E17"),sQuery(id+"F2.wireOp",EDGE,"E18"),sQuery(id+"F2.wireOp",EDGE,"E19"),sQuery(id+"F2.wireOp",EDGE,"E20.MirrorCS"),sQuery(id+"F2.wireOp",EDGE,"E21.MirrorCS"),sQuery(id+"F2.wireOp",EDGE,"E22.MirrorCS"),sQuery(id+"F2.wireOp",EDGE,"E23.MirrorCS"),sQuery(id+"F2.wireOp",EDGE,"E24.MirrorCS"),sQuery(id+"F2.wireOp",EDGE,"E25.MirrorCS")])],"isStart":false}),"instanceName":"2"})});
            var Q12;
            Q12=makeQuery(id+"F8.opChamfer","SPLIT",FACE,{"disambiguationData":[OD(0.0)],"derivedFrom":makeQuery(id+"F7.opPattern","COPY",FACE,{"derivedFrom":makeQuery(id+"F4.opExtrude","CAP_FACE",FACE,{"disambiguationData":[OSD([sQuery(id+"F2.wireOp",EDGE,"E9"),sQuery(id+"F2.wireOp",EDGE,"E10"),sQuery(id+"F2.wireOp",EDGE,"E11"),sQuery(id+"F2.wireOp",EDGE,"E12"),sQuery(id+"F2.wireOp",EDGE,"E13"),sQuery(id+"F2.wireOp",EDGE,"E14"),sQuery(id+"F2.wireOp",EDGE,"E15"),sQuery(id+"F2.wireOp",EDGE,"E17"),sQuery(id+"F2.wireOp",EDGE,"E18"),sQuery(id+"F2.wireOp",EDGE,"E19"),sQuery(id+"F2.wireOp",EDGE,"E20.MirrorCS"),sQuery(id+"F2.wireOp",EDGE,"E21.MirrorCS"),sQuery(id+"F2.wireOp",EDGE,"E22.MirrorCS"),sQuery(id+"F2.wireOp",EDGE,"E23.MirrorCS"),sQuery(id+"F2.wireOp",EDGE,"E24.MirrorCS"),sQuery(id+"F2.wireOp",EDGE,"E25.MirrorCS")])],"isStart":false}),"instanceName":"2"})});
            var Q13;
            Q13=makeQuery(id+"F8.opChamfer","SPLIT",FACE,{"disambiguationData":[OD(1.0)],"derivedFrom":makeQuery(id+"F7.opPattern","COPY",FACE,{"derivedFrom":makeQuery(id+"F4.opExtrude","CAP_FACE",FACE,{"disambiguationData":[OSD([sQuery(id+"F2.wireOp",EDGE,"E9"),sQuery(id+"F2.wireOp",EDGE,"E10"),sQuery(id+"F2.wireOp",EDGE,"E11"),sQuery(id+"F2.wireOp",EDGE,"E12"),sQuery(id+"F2.wireOp",EDGE,"E13"),sQuery(id+"F2.wireOp",EDGE,"E14"),sQuery(id+"F2.wireOp",EDGE,"E15"),sQuery(id+"F2.wireOp",EDGE,"E17"),sQuery(id+"F2.wireOp",EDGE,"E18"),sQuery(id+"F2.wireOp",EDGE,"E19"),sQuery(id+"F2.wireOp",EDGE,"E20.MirrorCS"),sQuery(id+"F2.wireOp",EDGE,"E21.MirrorCS"),sQuery(id+"F2.wireOp",EDGE,"E22.MirrorCS"),sQuery(id+"F2.wireOp",EDGE,"E23.MirrorCS"),sQuery(id+"F2.wireOp",EDGE,"E24.MirrorCS"),sQuery(id+"F2.wireOp",EDGE,"E25.MirrorCS")])],"isStart":false}),"instanceName":"2"})});
            var Q14;
            Q14=makeQuery(id+"F8.opChamfer","SPLIT",FACE,{"disambiguationData":[OD(2.0)],"derivedFrom":makeQuery(id+"F4.opExtrude","CAP_FACE",FACE,{"disambiguationData":[OSD([sQuery(id+"F2.wireOp",EDGE,"E9"),sQuery(id+"F2.wireOp",EDGE,"E10"),sQuery(id+"F2.wireOp",EDGE,"E11"),sQuery(id+"F2.wireOp",EDGE,"E12"),sQuery(id+"F2.wireOp",EDGE,"E13"),sQuery(id+"F2.wireOp",EDGE,"E14"),sQuery(id+"F2.wireOp",EDGE,"E15"),sQuery(id+"F2.wireOp",EDGE,"E17"),sQuery(id+"F2.wireOp",EDGE,"E18"),sQuery(id+"F2.wireOp",EDGE,"E19"),sQuery(id+"F2.wireOp",EDGE,"E20.MirrorCS"),sQuery(id+"F2.wireOp",EDGE,"E21.MirrorCS"),sQuery(id+"F2.wireOp",EDGE,"E22.MirrorCS"),sQuery(id+"F2.wireOp",EDGE,"E23.MirrorCS"),sQuery(id+"F2.wireOp",EDGE,"E24.MirrorCS"),sQuery(id+"F2.wireOp",EDGE,"E25.MirrorCS")])],"isStart":false})});
            fillet(context, id + "F10", {"entities" : qUnion([Q0, Q1, Q2, Q3, Q4, Q5, Q6, Q7, Q8, Q9, Q10, Q11, Q12, Q13, Q14]), "radius" : 2 * mm, "tangentPropagation" : true, "allowEdgeOverflow" : false});
        }
        {
            var Q0;
            {var subQ0=sQuery(id+"F1.wireOp",EDGE,"E1");Q0=makeQuery(id+"F8.opChamfer","TWEAK_EDGE",EDGE,{"derivedFrom":[makeQuery(id+"F7.boolean.opBoolean","TWEAK_VERTEX",VERTEX,{"derivedFrom":[makeQuery(id+"F3.opExtrude","CAP_FACE",FACE,{"disambiguationData":[OSD([sQuery(id+"F1.wireOp",EDGE,"E0"),subQ0])],"isStart":false}),makeQuery(id+"F3.opExtrude","SWEPT_FACE",FACE,{"disambiguationData":[OSD([subQ0])]}),makeQuery(id+"F4.opExtrude","SWEPT_FACE",FACE,{"disambiguationData":[OSD([sQuery(id+"F2.wireOp",EDGE,"E13"),sQuery(id+"F2.wireOp",EDGE,"E19"),sQuery(id+"F2.wireOp",EDGE,"E25.MirrorCS")])]}),makeQuery(id+"F4.opExtrude","SWEPT_FACE",FACE,{"disambiguationData":[OSD([sQuery(id+"F2.wireOp",EDGE,"E15")])]})]})]});}
            var Q1;
            {var subQ0=makeQuery(id+"F4.opExtrude","SWEPT_FACE",FACE,{"disambiguationData":[OSD([sQuery(id+"F2.wireOp",EDGE,"E13"),sQuery(id+"F2.wireOp",EDGE,"E19"),sQuery(id+"F2.wireOp",EDGE,"E25.MirrorCS")])]});var subQ1=sQuery(id+"F1.wireOp",EDGE,"E1");Q1=makeQuery(id+"F7.boolean.opBoolean","SPLIT",EDGE,{"disambiguationData":[TD([makeQuery(id+"F3.opExtrude","CAP_FACE",FACE,{"disambiguationData":[OSD([sQuery(id+"F1.wireOp",EDGE,"E0"),subQ1])],"isStart":false}),makeQuery(id+"F3.opExtrude","SWEPT_FACE",FACE,{"disambiguationData":[OSD([subQ1])]}),subQ0,makeQuery(id+"F4.opExtrude","SWEPT_FACE",FACE,{"disambiguationData":[OSD([sQuery(id+"F2.wireOp",EDGE,"E15")])]}),makeQuery(id+"F7.opPattern","COPY",FACE,{"derivedFrom":subQ0,"instanceName":"1"}),makeQuery(id+"F7.opPattern","COPY",FACE,{"derivedFrom":makeQuery(id+"F4.opExtrude","SWEPT_FACE",FACE,{"disambiguationData":[OSD([sQuery(id+"F2.wireOp",EDGE,"E22.MirrorCS")])]}),"instanceName":"1"})])],"derivedFrom":makeQuery(id+"F3.opExtrude","CAP_EDGE",EDGE,{"disambiguationData":[OSD([subQ1])],"isStart":false})});}
            var Q2;
            {var subQ0=sQuery(id+"F1.wireOp",EDGE,"E1");Q2=makeQuery(id+"F8.opChamfer","TWEAK_EDGE",EDGE,{"derivedFrom":[makeQuery(id+"F7.boolean.opBoolean","TWEAK_VERTEX",VERTEX,{"derivedFrom":[makeQuery(id+"F3.opExtrude","CAP_FACE",FACE,{"disambiguationData":[OSD([sQuery(id+"F1.wireOp",EDGE,"E0"),subQ0])],"isStart":false}),makeQuery(id+"F3.opExtrude","SWEPT_FACE",FACE,{"disambiguationData":[OSD([subQ0])]}),makeQuery(id+"F7.opPattern","COPY",FACE,{"derivedFrom":makeQuery(id+"F4.opExtrude","SWEPT_FACE",FACE,{"disambiguationData":[OSD([sQuery(id+"F2.wireOp",EDGE,"E13"),sQuery(id+"F2.wireOp",EDGE,"E19"),sQuery(id+"F2.wireOp",EDGE,"E25.MirrorCS")])]}),"instanceName":"1"}),makeQuery(id+"F7.opPattern","COPY",FACE,{"derivedFrom":makeQuery(id+"F4.opExtrude","SWEPT_FACE",FACE,{"disambiguationData":[OSD([sQuery(id+"F2.wireOp",EDGE,"E22.MirrorCS")])]}),"instanceName":"1"})]})]});}
            var Q3;
            {var subQ0=sQuery(id+"F1.wireOp",EDGE,"E1");var subQ1=sQuery(id+"F1.wireOp",EDGE,"E0");var subQ3=sQuery(id+"F2.wireOp",EDGE,"E19");var subQ5=sQuery(id+"F2.wireOp",EDGE,"E15");Q3=makeQuery(id+"F7.boolean.opBoolean","SPLIT",EDGE,{"disambiguationData":[TD([makeQuery(id+"F3.opExtrude","CAP_FACE",FACE,{"disambiguationData":[OSD([subQ1,subQ0])],"isStart":true})])],"derivedFrom":makeQuery(id+"F4.opExtrude","SWEPT_EDGE",EDGE,{"disambiguationData":[OSD([subQ5,subQ3])]})});}
            var Q4;
            {var subQ0=sQuery(id+"F1.wireOp",EDGE,"E1");var subQ1=sQuery(id+"F1.wireOp",EDGE,"E0");var subQ2=sQuery(id+"F2.wireOp",EDGE,"E25.MirrorCS");var subQ3=sQuery(id+"F2.wireOp",EDGE,"E22.MirrorCS");Q4=makeQuery(id+"F7.boolean.opBoolean","SPLIT",EDGE,{"disambiguationData":[TD([makeQuery(id+"F3.opExtrude","CAP_FACE",FACE,{"disambiguationData":[OSD([subQ1,subQ0])],"isStart":true})])],"derivedFrom":makeQuery(id+"F7.opPattern","COPY",EDGE,{"derivedFrom":makeQuery(id+"F4.opExtrude","SWEPT_EDGE",EDGE,{"disambiguationData":[OSD([subQ3,subQ2])]}),"instanceName":"1"})});}
            var Q5;
            {var subQ0=sQuery(id+"F1.wireOp",EDGE,"E1");Q5=makeQuery(id+"F8.opChamfer","TWEAK_EDGE",EDGE,{"derivedFrom":[makeQuery(id+"F7.boolean.opBoolean","TWEAK_VERTEX",VERTEX,{"derivedFrom":[makeQuery(id+"F3.opExtrude","CAP_FACE",FACE,{"disambiguationData":[OSD([sQuery(id+"F1.wireOp",EDGE,"E0"),subQ0])],"isStart":false}),makeQuery(id+"F3.opExtrude","SWEPT_FACE",FACE,{"disambiguationData":[OSD([subQ0])]}),makeQuery(id+"F7.opPattern","COPY",FACE,{"derivedFrom":makeQuery(id+"F4.opExtrude","SWEPT_FACE",FACE,{"disambiguationData":[OSD([sQuery(id+"F2.wireOp",EDGE,"E13"),sQuery(id+"F2.wireOp",EDGE,"E19"),sQuery(id+"F2.wireOp",EDGE,"E25.MirrorCS")])]}),"instanceName":"1"}),makeQuery(id+"F7.opPattern","COPY",FACE,{"derivedFrom":makeQuery(id+"F4.opExtrude","SWEPT_FACE",FACE,{"disambiguationData":[OSD([sQuery(id+"F2.wireOp",EDGE,"E15")])]}),"instanceName":"1"})]})]});}
            var Q6;
            {var subQ0=makeQuery(id+"F4.opExtrude","SWEPT_FACE",FACE,{"disambiguationData":[OSD([sQuery(id+"F2.wireOp",EDGE,"E13"),sQuery(id+"F2.wireOp",EDGE,"E19"),sQuery(id+"F2.wireOp",EDGE,"E25.MirrorCS")])]});var subQ1=sQuery(id+"F1.wireOp",EDGE,"E1");Q6=makeQuery(id+"F7.boolean.opBoolean","SPLIT",EDGE,{"disambiguationData":[TD([makeQuery(id+"F3.opExtrude","CAP_FACE",FACE,{"disambiguationData":[OSD([sQuery(id+"F1.wireOp",EDGE,"E0"),subQ1])],"isStart":false}),makeQuery(id+"F3.opExtrude","SWEPT_FACE",FACE,{"disambiguationData":[OSD([subQ1])]}),makeQuery(id+"F7.opPattern","COPY",FACE,{"derivedFrom":subQ0,"instanceName":"1"}),makeQuery(id+"F7.opPattern","COPY",FACE,{"derivedFrom":makeQuery(id+"F4.opExtrude","SWEPT_FACE",FACE,{"disambiguationData":[OSD([sQuery(id+"F2.wireOp",EDGE,"E15")])]}),"instanceName":"1"}),makeQuery(id+"F7.opPattern","COPY",FACE,{"derivedFrom":subQ0,"instanceName":"2"}),makeQuery(id+"F7.opPattern","COPY",FACE,{"derivedFrom":makeQuery(id+"F4.opExtrude","SWEPT_FACE",FACE,{"disambiguationData":[OSD([sQuery(id+"F2.wireOp",EDGE,"E22.MirrorCS")])]}),"instanceName":"2"})])],"derivedFrom":makeQuery(id+"F3.opExtrude","CAP_EDGE",EDGE,{"disambiguationData":[OSD([subQ1])],"isStart":false})});}
            var Q7;
            {var subQ0=sQuery(id+"F1.wireOp",EDGE,"E1");Q7=makeQuery(id+"F8.opChamfer","TWEAK_EDGE",EDGE,{"derivedFrom":[makeQuery(id+"F7.boolean.opBoolean","TWEAK_VERTEX",VERTEX,{"derivedFrom":[makeQuery(id+"F3.opExtrude","CAP_FACE",FACE,{"disambiguationData":[OSD([sQuery(id+"F1.wireOp",EDGE,"E0"),subQ0])],"isStart":false}),makeQuery(id+"F3.opExtrude","SWEPT_FACE",FACE,{"disambiguationData":[OSD([subQ0])]}),makeQuery(id+"F7.opPattern","COPY",FACE,{"derivedFrom":makeQuery(id+"F4.opExtrude","SWEPT_FACE",FACE,{"disambiguationData":[OSD([sQuery(id+"F2.wireOp",EDGE,"E13"),sQuery(id+"F2.wireOp",EDGE,"E19"),sQuery(id+"F2.wireOp",EDGE,"E25.MirrorCS")])]}),"instanceName":"2"}),makeQuery(id+"F7.opPattern","COPY",FACE,{"derivedFrom":makeQuery(id+"F4.opExtrude","SWEPT_FACE",FACE,{"disambiguationData":[OSD([sQuery(id+"F2.wireOp",EDGE,"E22.MirrorCS")])]}),"instanceName":"2"})]})]});}
            var Q8;
            {var subQ0=sQuery(id+"F1.wireOp",EDGE,"E1");var subQ1=sQuery(id+"F1.wireOp",EDGE,"E0");var subQ2=sQuery(id+"F2.wireOp",EDGE,"E25.MirrorCS");var subQ3=sQuery(id+"F2.wireOp",EDGE,"E22.MirrorCS");Q8=makeQuery(id+"F7.boolean.opBoolean","SPLIT",EDGE,{"disambiguationData":[TD([makeQuery(id+"F3.opExtrude","CAP_FACE",FACE,{"disambiguationData":[OSD([subQ1,subQ0])],"isStart":true})])],"derivedFrom":makeQuery(id+"F7.opPattern","COPY",EDGE,{"derivedFrom":makeQuery(id+"F4.opExtrude","SWEPT_EDGE",EDGE,{"disambiguationData":[OSD([subQ3,subQ2])]}),"instanceName":"2"})});}
            var Q9;
            {var subQ0=sQuery(id+"F1.wireOp",EDGE,"E1");var subQ1=sQuery(id+"F1.wireOp",EDGE,"E0");var subQ3=sQuery(id+"F2.wireOp",EDGE,"E19");var subQ4=sQuery(id+"F2.wireOp",EDGE,"E15");Q9=makeQuery(id+"F7.boolean.opBoolean","SPLIT",EDGE,{"disambiguationData":[TD([makeQuery(id+"F3.opExtrude","CAP_FACE",FACE,{"disambiguationData":[OSD([subQ1,subQ0])],"isStart":true})])],"derivedFrom":makeQuery(id+"F7.opPattern","COPY",EDGE,{"derivedFrom":makeQuery(id+"F4.opExtrude","SWEPT_EDGE",EDGE,{"disambiguationData":[OSD([subQ4,subQ3])]}),"instanceName":"1"})});}
            var Q10;
            {var subQ0=sQuery(id+"F1.wireOp",EDGE,"E1");var subQ1=sQuery(id+"F2.wireOp",EDGE,"E22.MirrorCS");var subQ2=sQuery(id+"F1.wireOp",EDGE,"E0");var subQ3=sQuery(id+"F2.wireOp",EDGE,"E25.MirrorCS");Q10=makeQuery(id+"F7.boolean.opBoolean","SPLIT",EDGE,{"disambiguationData":[TD([makeQuery(id+"F3.opExtrude","CAP_FACE",FACE,{"disambiguationData":[OSD([subQ2,subQ0])],"isStart":true})])],"derivedFrom":makeQuery(id+"F4.opExtrude","SWEPT_EDGE",EDGE,{"disambiguationData":[OSD([subQ1,subQ3])]})});}
            var Q11;
            {var subQ0=sQuery(id+"F1.wireOp",EDGE,"E1");var subQ1=sQuery(id+"F1.wireOp",EDGE,"E0");var subQ2=sQuery(id+"F2.wireOp",EDGE,"E15");var subQ4=sQuery(id+"F2.wireOp",EDGE,"E19");Q11=makeQuery(id+"F7.boolean.opBoolean","SPLIT",EDGE,{"disambiguationData":[TD([makeQuery(id+"F3.opExtrude","CAP_FACE",FACE,{"disambiguationData":[OSD([subQ1,subQ0])],"isStart":true})])],"derivedFrom":makeQuery(id+"F7.opPattern","COPY",EDGE,{"derivedFrom":makeQuery(id+"F4.opExtrude","SWEPT_EDGE",EDGE,{"disambiguationData":[OSD([subQ2,subQ4])]}),"instanceName":"2"})});}
            var Q12;
            {var subQ0=sQuery(id+"F1.wireOp",EDGE,"E1");var subQ1=makeQuery(id+"F4.opExtrude","SWEPT_FACE",FACE,{"disambiguationData":[OSD([sQuery(id+"F2.wireOp",EDGE,"E13"),sQuery(id+"F2.wireOp",EDGE,"E19"),sQuery(id+"F2.wireOp",EDGE,"E25.MirrorCS")])]});Q12=makeQuery(id+"F7.boolean.opBoolean","SPLIT",EDGE,{"disambiguationData":[TD([makeQuery(id+"F3.opExtrude","CAP_FACE",FACE,{"disambiguationData":[OSD([sQuery(id+"F1.wireOp",EDGE,"E0"),subQ0])],"isStart":false}),makeQuery(id+"F3.opExtrude","SWEPT_FACE",FACE,{"disambiguationData":[OSD([subQ0])]}),subQ1,makeQuery(id+"F4.opExtrude","SWEPT_FACE",FACE,{"disambiguationData":[OSD([sQuery(id+"F2.wireOp",EDGE,"E22.MirrorCS")])]}),makeQuery(id+"F7.opPattern","COPY",FACE,{"derivedFrom":subQ1,"instanceName":"2"}),makeQuery(id+"F7.opPattern","COPY",FACE,{"derivedFrom":makeQuery(id+"F4.opExtrude","SWEPT_FACE",FACE,{"disambiguationData":[OSD([sQuery(id+"F2.wireOp",EDGE,"E15")])]}),"instanceName":"2"})])],"derivedFrom":makeQuery(id+"F3.opExtrude","CAP_EDGE",EDGE,{"disambiguationData":[OSD([subQ0])],"isStart":false})});}
            var Q13;
            {var subQ0=sQuery(id+"F1.wireOp",EDGE,"E1");Q13=makeQuery(id+"F8.opChamfer","TWEAK_EDGE",EDGE,{"derivedFrom":[makeQuery(id+"F7.boolean.opBoolean","TWEAK_VERTEX",VERTEX,{"derivedFrom":[makeQuery(id+"F3.opExtrude","CAP_FACE",FACE,{"disambiguationData":[OSD([sQuery(id+"F1.wireOp",EDGE,"E0"),subQ0])],"isStart":false}),makeQuery(id+"F3.opExtrude","SWEPT_FACE",FACE,{"disambiguationData":[OSD([subQ0])]}),makeQuery(id+"F4.opExtrude","SWEPT_FACE",FACE,{"disambiguationData":[OSD([sQuery(id+"F2.wireOp",EDGE,"E13"),sQuery(id+"F2.wireOp",EDGE,"E19"),sQuery(id+"F2.wireOp",EDGE,"E25.MirrorCS")])]}),makeQuery(id+"F4.opExtrude","SWEPT_FACE",FACE,{"disambiguationData":[OSD([sQuery(id+"F2.wireOp",EDGE,"E22.MirrorCS")])]})]})]});}
            var Q14;
            {var subQ0=sQuery(id+"F1.wireOp",EDGE,"E1");Q14=makeQuery(id+"F8.opChamfer","TWEAK_EDGE",EDGE,{"derivedFrom":[makeQuery(id+"F7.boolean.opBoolean","TWEAK_VERTEX",VERTEX,{"derivedFrom":[makeQuery(id+"F3.opExtrude","CAP_FACE",FACE,{"disambiguationData":[OSD([sQuery(id+"F1.wireOp",EDGE,"E0"),subQ0])],"isStart":false}),makeQuery(id+"F3.opExtrude","SWEPT_FACE",FACE,{"disambiguationData":[OSD([subQ0])]}),makeQuery(id+"F7.opPattern","COPY",FACE,{"derivedFrom":makeQuery(id+"F4.opExtrude","SWEPT_FACE",FACE,{"disambiguationData":[OSD([sQuery(id+"F2.wireOp",EDGE,"E13"),sQuery(id+"F2.wireOp",EDGE,"E19"),sQuery(id+"F2.wireOp",EDGE,"E25.MirrorCS")])]}),"instanceName":"2"}),makeQuery(id+"F7.opPattern","COPY",FACE,{"derivedFrom":makeQuery(id+"F4.opExtrude","SWEPT_FACE",FACE,{"disambiguationData":[OSD([sQuery(id+"F2.wireOp",EDGE,"E15")])]}),"instanceName":"2"})]})]});}
            fillet(context, id + "F11", {"entities" : qUnion([Q0, Q1, Q2, Q3, Q4, Q5, Q6, Q7, Q8, Q9, Q10, Q11, Q12, Q13, Q14]), "radius" : 2 * mm, "tangentPropagation" : true, "allowEdgeOverflow" : false});
        }
        {
            var Q0;
            Q0=makeQuery(id+"F7.opPattern","COPY",EDGE,{"derivedFrom":makeQuery(id+"F4.opExtrude","CAP_EDGE",EDGE,{"disambiguationData":[OSD([sQuery(id+"F2.wireOp",EDGE,"E21.MirrorCS")])],"isStart":true}),"instanceName":"2"});
            var Q1;
            Q1=makeQuery(id+"F7.opPattern","COPY",EDGE,{"derivedFrom":makeQuery(id+"F4.opExtrude","CAP_EDGE",EDGE,{"disambiguationData":[OSD([sQuery(id+"F2.wireOp",EDGE,"E10")])],"isStart":true}),"instanceName":"2"});
            var Q2;
            Q2=makeQuery(id+"F7.opPattern","COPY",EDGE,{"derivedFrom":makeQuery(id+"F4.opExtrude","CAP_EDGE",EDGE,{"disambiguationData":[OSD([sQuery(id+"F2.wireOp",EDGE,"E12")])],"isStart":true}),"instanceName":"2"});
            var Q3;
            Q3=makeQuery(id+"F7.opPattern","COPY",EDGE,{"derivedFrom":makeQuery(id+"F4.opExtrude","CAP_EDGE",EDGE,{"disambiguationData":[OSD([sQuery(id+"F2.wireOp",EDGE,"E12")])],"isStart":true}),"instanceName":"1"});
            var Q4;
            Q4=makeQuery(id+"F7.opPattern","COPY",EDGE,{"derivedFrom":makeQuery(id+"F4.opExtrude","CAP_EDGE",EDGE,{"disambiguationData":[OSD([sQuery(id+"F2.wireOp",EDGE,"E10")])],"isStart":true}),"instanceName":"1"});
            var Q5;
            Q5=makeQuery(id+"F7.opPattern","COPY",EDGE,{"derivedFrom":makeQuery(id+"F4.opExtrude","CAP_EDGE",EDGE,{"disambiguationData":[OSD([sQuery(id+"F2.wireOp",EDGE,"E21.MirrorCS")])],"isStart":true}),"instanceName":"1"});
            var Q6;
            Q6=makeQuery(id+"F4.opExtrude","CAP_EDGE",EDGE,{"disambiguationData":[OSD([sQuery(id+"F2.wireOp",EDGE,"E12")])],"isStart":true});
            var Q7;
            Q7=makeQuery(id+"F4.opExtrude","CAP_EDGE",EDGE,{"disambiguationData":[OSD([sQuery(id+"F2.wireOp",EDGE,"E10")])],"isStart":true});
            var Q8;
            Q8=makeQuery(id+"F4.opExtrude","CAP_EDGE",EDGE,{"disambiguationData":[OSD([sQuery(id+"F2.wireOp",EDGE,"E21.MirrorCS")])],"isStart":true});
            chamfer(context, id + "F12", {"entities" : qUnion([Q0, Q1, Q2, Q3, Q4, Q5, Q6, Q7, Q8]), "width" : 6 * mm, "tangentPropagation" : true});
        }
        {
            var Q0;
            {var subQ0=sQuery(id+"F2.wireOp",EDGE,"E10");Q0=makeQuery(id+"F12.opChamfer","BLEND_EDGE",EDGE,{"blendedFrom":[makeQuery(id+"F7.opPattern","COPY",EDGE,{"derivedFrom":makeQuery(id+"F4.opExtrude","CAP_EDGE",EDGE,{"disambiguationData":[OSD([subQ0])],"isStart":true}),"instanceName":"1"}),makeQuery(id+"F7.opPattern","COPY",FACE,{"derivedFrom":makeQuery(id+"F4.opExtrude","SWEPT_FACE",FACE,{"disambiguationData":[OSD([subQ0])]}),"instanceName":"1"})],"blendedInto":[makeQuery(id+"F7.opPattern","COPY",FACE,{"derivedFrom":makeQuery(id+"F4.opExtrude","SWEPT_FACE",FACE,{"disambiguationData":[OSD([subQ0])]}),"instanceName":"1"})]});}
            var Q1;
            {var subQ0=sQuery(id+"F2.wireOp",EDGE,"E12");Q1=makeQuery(id+"F12.opChamfer","BLEND_EDGE",EDGE,{"blendedFrom":[makeQuery(id+"F7.opPattern","COPY",EDGE,{"derivedFrom":makeQuery(id+"F4.opExtrude","CAP_EDGE",EDGE,{"disambiguationData":[OSD([subQ0])],"isStart":true}),"instanceName":"1"}),makeQuery(id+"F7.opPattern","COPY",FACE,{"derivedFrom":makeQuery(id+"F4.opExtrude","SWEPT_FACE",FACE,{"disambiguationData":[OSD([subQ0])]}),"instanceName":"1"})],"blendedInto":[makeQuery(id+"F7.opPattern","COPY",FACE,{"derivedFrom":makeQuery(id+"F4.opExtrude","SWEPT_FACE",FACE,{"disambiguationData":[OSD([subQ0])]}),"instanceName":"1"})]});}
            var Q2;
            {var subQ0=sQuery(id+"F2.wireOp",EDGE,"E21.MirrorCS");Q2=makeQuery(id+"F12.opChamfer","BLEND_EDGE",EDGE,{"blendedFrom":[makeQuery(id+"F7.opPattern","COPY",EDGE,{"derivedFrom":makeQuery(id+"F4.opExtrude","CAP_EDGE",EDGE,{"disambiguationData":[OSD([subQ0])],"isStart":true}),"instanceName":"1"}),makeQuery(id+"F7.opPattern","COPY",FACE,{"derivedFrom":makeQuery(id+"F4.opExtrude","SWEPT_FACE",FACE,{"disambiguationData":[OSD([subQ0])]}),"instanceName":"1"})],"blendedInto":[makeQuery(id+"F7.opPattern","COPY",FACE,{"derivedFrom":makeQuery(id+"F4.opExtrude","SWEPT_FACE",FACE,{"disambiguationData":[OSD([subQ0])]}),"instanceName":"1"})]});}
            var Q3;
            {var subQ0=sQuery(id+"F2.wireOp",EDGE,"E12");Q3=makeQuery(id+"F12.opChamfer","BLEND_EDGE",EDGE,{"blendedFrom":[makeQuery(id+"F4.opExtrude","CAP_EDGE",EDGE,{"disambiguationData":[OSD([subQ0])],"isStart":true}),makeQuery(id+"F4.opExtrude","SWEPT_FACE",FACE,{"disambiguationData":[OSD([subQ0])]})],"blendedInto":[makeQuery(id+"F4.opExtrude","SWEPT_FACE",FACE,{"disambiguationData":[OSD([subQ0])]})]});}
            var Q4;
            {var subQ0=sQuery(id+"F2.wireOp",EDGE,"E10");Q4=makeQuery(id+"F12.opChamfer","BLEND_EDGE",EDGE,{"blendedFrom":[makeQuery(id+"F4.opExtrude","CAP_EDGE",EDGE,{"disambiguationData":[OSD([subQ0])],"isStart":true}),makeQuery(id+"F4.opExtrude","SWEPT_FACE",FACE,{"disambiguationData":[OSD([subQ0])]})],"blendedInto":[makeQuery(id+"F4.opExtrude","SWEPT_FACE",FACE,{"disambiguationData":[OSD([subQ0])]})]});}
            var Q5;
            {var subQ0=sQuery(id+"F2.wireOp",EDGE,"E21.MirrorCS");Q5=makeQuery(id+"F12.opChamfer","BLEND_EDGE",EDGE,{"blendedFrom":[makeQuery(id+"F4.opExtrude","CAP_EDGE",EDGE,{"disambiguationData":[OSD([subQ0])],"isStart":true}),makeQuery(id+"F4.opExtrude","SWEPT_FACE",FACE,{"disambiguationData":[OSD([subQ0])]})],"blendedInto":[makeQuery(id+"F4.opExtrude","SWEPT_FACE",FACE,{"disambiguationData":[OSD([subQ0])]})]});}
            var Q6;
            {var subQ0=sQuery(id+"F2.wireOp",EDGE,"E12");Q6=makeQuery(id+"F12.opChamfer","BLEND_EDGE",EDGE,{"blendedFrom":[makeQuery(id+"F7.opPattern","COPY",EDGE,{"derivedFrom":makeQuery(id+"F4.opExtrude","CAP_EDGE",EDGE,{"disambiguationData":[OSD([subQ0])],"isStart":true}),"instanceName":"2"}),makeQuery(id+"F7.opPattern","COPY",FACE,{"derivedFrom":makeQuery(id+"F4.opExtrude","SWEPT_FACE",FACE,{"disambiguationData":[OSD([subQ0])]}),"instanceName":"2"})],"blendedInto":[makeQuery(id+"F7.opPattern","COPY",FACE,{"derivedFrom":makeQuery(id+"F4.opExtrude","SWEPT_FACE",FACE,{"disambiguationData":[OSD([subQ0])]}),"instanceName":"2"})]});}
            var Q7;
            {var subQ0=sQuery(id+"F2.wireOp",EDGE,"E10");Q7=makeQuery(id+"F12.opChamfer","BLEND_EDGE",EDGE,{"blendedFrom":[makeQuery(id+"F7.opPattern","COPY",EDGE,{"derivedFrom":makeQuery(id+"F4.opExtrude","CAP_EDGE",EDGE,{"disambiguationData":[OSD([subQ0])],"isStart":true}),"instanceName":"2"}),makeQuery(id+"F7.opPattern","COPY",FACE,{"derivedFrom":makeQuery(id+"F4.opExtrude","SWEPT_FACE",FACE,{"disambiguationData":[OSD([subQ0])]}),"instanceName":"2"})],"blendedInto":[makeQuery(id+"F7.opPattern","COPY",FACE,{"derivedFrom":makeQuery(id+"F4.opExtrude","SWEPT_FACE",FACE,{"disambiguationData":[OSD([subQ0])]}),"instanceName":"2"})]});}
            var Q8;
            {var subQ0=sQuery(id+"F2.wireOp",EDGE,"E21.MirrorCS");Q8=makeQuery(id+"F12.opChamfer","BLEND_EDGE",EDGE,{"blendedFrom":[makeQuery(id+"F7.opPattern","COPY",EDGE,{"derivedFrom":makeQuery(id+"F4.opExtrude","CAP_EDGE",EDGE,{"disambiguationData":[OSD([subQ0])],"isStart":true}),"instanceName":"2"}),makeQuery(id+"F7.opPattern","COPY",FACE,{"derivedFrom":makeQuery(id+"F4.opExtrude","SWEPT_FACE",FACE,{"disambiguationData":[OSD([subQ0])]}),"instanceName":"2"})],"blendedInto":[makeQuery(id+"F7.opPattern","COPY",FACE,{"derivedFrom":makeQuery(id+"F4.opExtrude","SWEPT_FACE",FACE,{"disambiguationData":[OSD([subQ0])]}),"instanceName":"2"})]});}
            fillet(context, id + "F13", {"entities" : qUnion([Q0, Q1, Q2, Q3, Q4, Q5, Q6, Q7, Q8]), "radius" : 5 * mm, "tangentPropagation" : true, "allowEdgeOverflow" : false});
        }
        {
            var Q0;
            Q0=makeQuery(id+"F4.opExtrude","SWEPT_FACE",FACE,{"disambiguationData":[OSD([sQuery(id+"F2.wireOp",EDGE,"E11")])]});
            cPlane(context, id + "F14", {"entities" : qUnion([Q0]), "cplaneType" : CPlaneType.OFFSET, "offset" : 4 * mm, "oppositeDirection" : true, "width" : 150 * mm, "height" : 150 * mm});
        }
        {
            var Q0;
            Q0=qCreatedBy(id+"F14.planeOp",FACE);
            var sketch = newSketch(context, id + "F15", { "sketchPlane" : qUnion([Q0])});
            skCircle(sketch, "E27", {"center": v(-41, 9.5) * mm, "radius": 3.1 * mm});
            skLineSegment(sketch, "E28", {"start": v(-37.9, 9.5) * mm, "end": v(-37.9, 15.05) * mm});
            skLineSegment(sketch, "E29", {"start": v(-37.9, 15.05) * mm, "end": v(-44.1, 15.05) * mm});
            skLineSegment(sketch, "E30", {"start": v(-44.1, 15.05) * mm, "end": v(-44.1, 9.5) * mm});
            skSolve(sketch);
        }
        {
            var Q0;
            Q0=qSketchRegion(id+"F15",true);
            extrude(context, id + "F16", {"entities" : qUnion([Q0]), "oppositeDirection" : true, "depth" : 4 * mm});
        }
        {
            var Q0;
            Q0=makeQuery(id+"F16.opExtrude","SWEPT_BODY",BODY,{"disambiguationData":[OSD([sQuery(id+"F15.wireOp",EDGE,"E27"),sQuery(id+"F15.wireOp",EDGE,"E28"),sQuery(id+"F15.wireOp",EDGE,"E29"),sQuery(id+"F15.wireOp",EDGE,"E30")])]});
            var Q1;
            Q1=qCreatedBy(makeId("Right.planeOp"),FACE);
            mirror(context, id + "F17", {"entities" : qUnion([Q0]), "mirrorPlane" : qUnion([Q1])});
        }
        {
            var Q0;
            Q0=makeQuery(id+"F17.opPattern","COPY",BODY,{"derivedFrom":makeQuery(id+"F16.opExtrude","SWEPT_BODY",BODY,{"disambiguationData":[OSD([sQuery(id+"F15.wireOp",EDGE,"E27"),sQuery(id+"F15.wireOp",EDGE,"E28"),sQuery(id+"F15.wireOp",EDGE,"E29"),sQuery(id+"F15.wireOp",EDGE,"E30")])]}),"instanceName":"1"});
            var Q1;
            Q1=makeQuery(id+"F16.opExtrude","SWEPT_BODY",BODY,{"disambiguationData":[OSD([sQuery(id+"F15.wireOp",EDGE,"E27"),sQuery(id+"F15.wireOp",EDGE,"E28"),sQuery(id+"F15.wireOp",EDGE,"E29"),sQuery(id+"F15.wireOp",EDGE,"E30")])]});
            var Q2;
            Q2=makeQuery(id+"F3.opExtrude","SWEPT_FACE",FACE,{"disambiguationData":[OSD([sQuery(id+"F1.wireOp",EDGE,"E0")])]});
            circularPattern(context, id + "F18", {"operationType" : NewBodyOperationType.REMOVE, "entities" : qUnion([Q0, Q1]), "axis" : qUnion([Q2]), "angle" : 120 * degree, "instanceCount" : 3});
        }
        {
            var Q0;
            {var subQ0=sQuery(id+"F2.wireOp",EDGE,"E10");Q0=makeQuery(id+"F18.boolean.opBoolean","INTERSECT",EDGE,{"derivedFrom":[makeQuery(id+"F10.opFillet","BLEND_FACE",FACE,{"disambiguationData":[OSD([subQ0]),TDD([makeQuery(id+"F4.opExtrude","CAP_EDGE",EDGE,{"disambiguationData":[OSD([subQ0])],"isStart":false})])]}),makeQuery(id+"F17.opPattern","COPY",FACE,{"derivedFrom":makeQuery(id+"F16.opExtrude","SWEPT_FACE",FACE,{"disambiguationData":[OSD([sQuery(id+"F15.wireOp",EDGE,"E30")])]}),"instanceName":"1"})]});}
            var Q1;
            {var subQ0=sQuery(id+"F2.wireOp",EDGE,"E25.MirrorCS");var subQ1=sQuery(id+"F2.wireOp",EDGE,"E19");var subQ2=sQuery(id+"F2.wireOp",EDGE,"E13");Q1=makeQuery(id+"F18.boolean.opBoolean","INTERSECT",EDGE,{"derivedFrom":[makeQuery(id+"F9.opFillet","SPLIT",FACE,{"disambiguationData":[OD(0.0)],"derivedFrom":makeQuery(id+"F8.opChamfer","BLEND_FACE",FACE,{"disambiguationData":[OSD([subQ2,subQ1,subQ0]),TDD([makeQuery(id+"F4.opExtrude","CAP_EDGE",EDGE,{"disambiguationData":[OSD([subQ2,subQ1,subQ0])],"isStart":false})])]})}),makeQuery(id+"F17.opPattern","COPY",FACE,{"derivedFrom":makeQuery(id+"F16.opExtrude","SWEPT_FACE",FACE,{"disambiguationData":[OSD([sQuery(id+"F15.wireOp",EDGE,"E28")])]}),"instanceName":"1"})]});}
            var Q2;
            {var subQ0=sQuery(id+"F2.wireOp",EDGE,"E25.MirrorCS");var subQ1=sQuery(id+"F2.wireOp",EDGE,"E19");var subQ2=sQuery(id+"F2.wireOp",EDGE,"E13");Q2=makeQuery(id+"F18.boolean.opBoolean","INTERSECT",EDGE,{"derivedFrom":[makeQuery(id+"F9.opFillet","SPLIT",FACE,{"disambiguationData":[OD(0.0)],"derivedFrom":makeQuery(id+"F8.opChamfer","BLEND_FACE",FACE,{"disambiguationData":[OSD([subQ2,subQ1,subQ0]),TDD([makeQuery(id+"F4.opExtrude","CAP_EDGE",EDGE,{"disambiguationData":[OSD([subQ2,subQ1,subQ0])],"isStart":false})])]})}),makeQuery(id+"F16.opExtrude","SWEPT_FACE",FACE,{"disambiguationData":[OSD([sQuery(id+"F15.wireOp",EDGE,"E28")])]})]});}
            var Q3;
            {var subQ0=sQuery(id+"F2.wireOp",EDGE,"E10");Q3=makeQuery(id+"F18.boolean.opBoolean","INTERSECT",EDGE,{"derivedFrom":[makeQuery(id+"F10.opFillet","BLEND_FACE",FACE,{"disambiguationData":[OSD([subQ0]),TDD([makeQuery(id+"F4.opExtrude","CAP_EDGE",EDGE,{"disambiguationData":[OSD([subQ0])],"isStart":false})])]}),makeQuery(id+"F16.opExtrude","SWEPT_FACE",FACE,{"disambiguationData":[OSD([sQuery(id+"F15.wireOp",EDGE,"E30")])]})]});}
            var Q4;
            Q4=makeQuery(id+"F18.boolean.opBoolean","INTERSECT",EDGE,{"derivedFrom":[makeQuery(id+"F8.opChamfer","SPLIT",FACE,{"disambiguationData":[OD(0.0)],"derivedFrom":makeQuery(id+"F4.opExtrude","CAP_FACE",FACE,{"disambiguationData":[OSD([sQuery(id+"F2.wireOp",EDGE,"E9"),sQuery(id+"F2.wireOp",EDGE,"E10"),sQuery(id+"F2.wireOp",EDGE,"E11"),sQuery(id+"F2.wireOp",EDGE,"E12"),sQuery(id+"F2.wireOp",EDGE,"E13"),sQuery(id+"F2.wireOp",EDGE,"E14"),sQuery(id+"F2.wireOp",EDGE,"E15"),sQuery(id+"F2.wireOp",EDGE,"E17"),sQuery(id+"F2.wireOp",EDGE,"E18"),sQuery(id+"F2.wireOp",EDGE,"E19"),sQuery(id+"F2.wireOp",EDGE,"E20.MirrorCS"),sQuery(id+"F2.wireOp",EDGE,"E21.MirrorCS"),sQuery(id+"F2.wireOp",EDGE,"E22.MirrorCS"),sQuery(id+"F2.wireOp",EDGE,"E23.MirrorCS"),sQuery(id+"F2.wireOp",EDGE,"E24.MirrorCS"),sQuery(id+"F2.wireOp",EDGE,"E25.MirrorCS")])],"isStart":false})}),makeQuery(id+"F16.opExtrude","CAP_FACE",FACE,{"disambiguationData":[OSD([sQuery(id+"F15.wireOp",EDGE,"E27"),sQuery(id+"F15.wireOp",EDGE,"E28"),sQuery(id+"F15.wireOp",EDGE,"E29"),sQuery(id+"F15.wireOp",EDGE,"E30")])],"isStart":false})]});
            var Q5;
            Q5=makeQuery(id+"F18.boolean.opBoolean","INTERSECT",EDGE,{"derivedFrom":[makeQuery(id+"F8.opChamfer","SPLIT",FACE,{"disambiguationData":[OD(0.0)],"derivedFrom":makeQuery(id+"F4.opExtrude","CAP_FACE",FACE,{"disambiguationData":[OSD([sQuery(id+"F2.wireOp",EDGE,"E9"),sQuery(id+"F2.wireOp",EDGE,"E10"),sQuery(id+"F2.wireOp",EDGE,"E11"),sQuery(id+"F2.wireOp",EDGE,"E12"),sQuery(id+"F2.wireOp",EDGE,"E13"),sQuery(id+"F2.wireOp",EDGE,"E14"),sQuery(id+"F2.wireOp",EDGE,"E15"),sQuery(id+"F2.wireOp",EDGE,"E17"),sQuery(id+"F2.wireOp",EDGE,"E18"),sQuery(id+"F2.wireOp",EDGE,"E19"),sQuery(id+"F2.wireOp",EDGE,"E20.MirrorCS"),sQuery(id+"F2.wireOp",EDGE,"E21.MirrorCS"),sQuery(id+"F2.wireOp",EDGE,"E22.MirrorCS"),sQuery(id+"F2.wireOp",EDGE,"E23.MirrorCS"),sQuery(id+"F2.wireOp",EDGE,"E24.MirrorCS"),sQuery(id+"F2.wireOp",EDGE,"E25.MirrorCS")])],"isStart":false})}),makeQuery(id+"F16.opExtrude","CAP_FACE",FACE,{"disambiguationData":[OSD([sQuery(id+"F15.wireOp",EDGE,"E27"),sQuery(id+"F15.wireOp",EDGE,"E28"),sQuery(id+"F15.wireOp",EDGE,"E29"),sQuery(id+"F15.wireOp",EDGE,"E30")])],"isStart":true})]});
            var Q6;
            Q6=makeQuery(id+"F18.boolean.opBoolean","INTERSECT",EDGE,{"derivedFrom":[makeQuery(id+"F8.opChamfer","SPLIT",FACE,{"disambiguationData":[OD(0.0)],"derivedFrom":makeQuery(id+"F4.opExtrude","CAP_FACE",FACE,{"disambiguationData":[OSD([sQuery(id+"F2.wireOp",EDGE,"E9"),sQuery(id+"F2.wireOp",EDGE,"E10"),sQuery(id+"F2.wireOp",EDGE,"E11"),sQuery(id+"F2.wireOp",EDGE,"E12"),sQuery(id+"F2.wireOp",EDGE,"E13"),sQuery(id+"F2.wireOp",EDGE,"E14"),sQuery(id+"F2.wireOp",EDGE,"E15"),sQuery(id+"F2.wireOp",EDGE,"E17"),sQuery(id+"F2.wireOp",EDGE,"E18"),sQuery(id+"F2.wireOp",EDGE,"E19"),sQuery(id+"F2.wireOp",EDGE,"E20.MirrorCS"),sQuery(id+"F2.wireOp",EDGE,"E21.MirrorCS"),sQuery(id+"F2.wireOp",EDGE,"E22.MirrorCS"),sQuery(id+"F2.wireOp",EDGE,"E23.MirrorCS"),sQuery(id+"F2.wireOp",EDGE,"E24.MirrorCS"),sQuery(id+"F2.wireOp",EDGE,"E25.MirrorCS")])],"isStart":false})}),makeQuery(id+"F17.opPattern","COPY",FACE,{"derivedFrom":makeQuery(id+"F16.opExtrude","CAP_FACE",FACE,{"disambiguationData":[OSD([sQuery(id+"F15.wireOp",EDGE,"E27"),sQuery(id+"F15.wireOp",EDGE,"E28"),sQuery(id+"F15.wireOp",EDGE,"E29"),sQuery(id+"F15.wireOp",EDGE,"E30")])],"isStart":false}),"instanceName":"1"})]});
            var Q7;
            Q7=makeQuery(id+"F18.boolean.opBoolean","INTERSECT",EDGE,{"derivedFrom":[makeQuery(id+"F8.opChamfer","SPLIT",FACE,{"disambiguationData":[OD(0.0)],"derivedFrom":makeQuery(id+"F4.opExtrude","CAP_FACE",FACE,{"disambiguationData":[OSD([sQuery(id+"F2.wireOp",EDGE,"E9"),sQuery(id+"F2.wireOp",EDGE,"E10"),sQuery(id+"F2.wireOp",EDGE,"E11"),sQuery(id+"F2.wireOp",EDGE,"E12"),sQuery(id+"F2.wireOp",EDGE,"E13"),sQuery(id+"F2.wireOp",EDGE,"E14"),sQuery(id+"F2.wireOp",EDGE,"E15"),sQuery(id+"F2.wireOp",EDGE,"E17"),sQuery(id+"F2.wireOp",EDGE,"E18"),sQuery(id+"F2.wireOp",EDGE,"E19"),sQuery(id+"F2.wireOp",EDGE,"E20.MirrorCS"),sQuery(id+"F2.wireOp",EDGE,"E21.MirrorCS"),sQuery(id+"F2.wireOp",EDGE,"E22.MirrorCS"),sQuery(id+"F2.wireOp",EDGE,"E23.MirrorCS"),sQuery(id+"F2.wireOp",EDGE,"E24.MirrorCS"),sQuery(id+"F2.wireOp",EDGE,"E25.MirrorCS")])],"isStart":false})}),makeQuery(id+"F17.opPattern","COPY",FACE,{"derivedFrom":makeQuery(id+"F16.opExtrude","CAP_FACE",FACE,{"disambiguationData":[OSD([sQuery(id+"F15.wireOp",EDGE,"E27"),sQuery(id+"F15.wireOp",EDGE,"E28"),sQuery(id+"F15.wireOp",EDGE,"E29"),sQuery(id+"F15.wireOp",EDGE,"E30")])],"isStart":true}),"instanceName":"1"})]});
            var Q8;
            {var subQ0=sQuery(id+"F2.wireOp",EDGE,"E10");Q8=makeQuery(id+"F18.boolean.opBoolean","INTERSECT",EDGE,{"derivedFrom":[makeQuery(id+"F10.opFillet","BLEND_FACE",FACE,{"disambiguationData":[OSD([subQ0]),TDD([makeQuery(id+"F7.opPattern","COPY",EDGE,{"derivedFrom":makeQuery(id+"F4.opExtrude","CAP_EDGE",EDGE,{"disambiguationData":[OSD([subQ0])],"isStart":false}),"instanceName":"2"})])]}),makeQuery(id+"F18.opPattern","COPY",FACE,{"derivedFrom":makeQuery(id+"F17.opPattern","COPY",FACE,{"derivedFrom":makeQuery(id+"F16.opExtrude","SWEPT_FACE",FACE,{"disambiguationData":[OSD([sQuery(id+"F15.wireOp",EDGE,"E30")])]}),"instanceName":"1"}),"instanceName":"1"})]});}
            var Q9;
            {var subQ0=sQuery(id+"F2.wireOp",EDGE,"E25.MirrorCS");var subQ1=sQuery(id+"F2.wireOp",EDGE,"E19");var subQ2=sQuery(id+"F2.wireOp",EDGE,"E13");Q9=makeQuery(id+"F18.boolean.opBoolean","INTERSECT",EDGE,{"derivedFrom":[makeQuery(id+"F9.opFillet","SPLIT",FACE,{"disambiguationData":[OD(0.0)],"derivedFrom":makeQuery(id+"F8.opChamfer","BLEND_FACE",FACE,{"disambiguationData":[OSD([subQ2,subQ1,subQ0]),TDD([makeQuery(id+"F7.opPattern","COPY",EDGE,{"derivedFrom":makeQuery(id+"F4.opExtrude","CAP_EDGE",EDGE,{"disambiguationData":[OSD([subQ2,subQ1,subQ0])],"isStart":false}),"instanceName":"2"})])]})}),makeQuery(id+"F18.opPattern","COPY",FACE,{"derivedFrom":makeQuery(id+"F17.opPattern","COPY",FACE,{"derivedFrom":makeQuery(id+"F16.opExtrude","SWEPT_FACE",FACE,{"disambiguationData":[OSD([sQuery(id+"F15.wireOp",EDGE,"E28")])]}),"instanceName":"1"}),"instanceName":"1"})]});}
            var Q10;
            Q10=makeQuery(id+"F18.boolean.opBoolean","INTERSECT",EDGE,{"derivedFrom":[makeQuery(id+"F8.opChamfer","SPLIT",FACE,{"disambiguationData":[OD(0.0)],"derivedFrom":makeQuery(id+"F7.opPattern","COPY",FACE,{"derivedFrom":makeQuery(id+"F4.opExtrude","CAP_FACE",FACE,{"disambiguationData":[OSD([sQuery(id+"F2.wireOp",EDGE,"E9"),sQuery(id+"F2.wireOp",EDGE,"E10"),sQuery(id+"F2.wireOp",EDGE,"E11"),sQuery(id+"F2.wireOp",EDGE,"E12"),sQuery(id+"F2.wireOp",EDGE,"E13"),sQuery(id+"F2.wireOp",EDGE,"E14"),sQuery(id+"F2.wireOp",EDGE,"E15"),sQuery(id+"F2.wireOp",EDGE,"E17"),sQuery(id+"F2.wireOp",EDGE,"E18"),sQuery(id+"F2.wireOp",EDGE,"E19"),sQuery(id+"F2.wireOp",EDGE,"E20.MirrorCS"),sQuery(id+"F2.wireOp",EDGE,"E21.MirrorCS"),sQuery(id+"F2.wireOp",EDGE,"E22.MirrorCS"),sQuery(id+"F2.wireOp",EDGE,"E23.MirrorCS"),sQuery(id+"F2.wireOp",EDGE,"E24.MirrorCS"),sQuery(id+"F2.wireOp",EDGE,"E25.MirrorCS")])],"isStart":false}),"instanceName":"2"})}),makeQuery(id+"F18.opPattern","COPY",FACE,{"derivedFrom":makeQuery(id+"F17.opPattern","COPY",FACE,{"derivedFrom":makeQuery(id+"F16.opExtrude","CAP_FACE",FACE,{"disambiguationData":[OSD([sQuery(id+"F15.wireOp",EDGE,"E27"),sQuery(id+"F15.wireOp",EDGE,"E28"),sQuery(id+"F15.wireOp",EDGE,"E29"),sQuery(id+"F15.wireOp",EDGE,"E30")])],"isStart":false}),"instanceName":"1"}),"instanceName":"1"})]});
            var Q11;
            Q11=makeQuery(id+"F18.boolean.opBoolean","INTERSECT",EDGE,{"derivedFrom":[makeQuery(id+"F8.opChamfer","SPLIT",FACE,{"disambiguationData":[OD(0.0)],"derivedFrom":makeQuery(id+"F7.opPattern","COPY",FACE,{"derivedFrom":makeQuery(id+"F4.opExtrude","CAP_FACE",FACE,{"disambiguationData":[OSD([sQuery(id+"F2.wireOp",EDGE,"E9"),sQuery(id+"F2.wireOp",EDGE,"E10"),sQuery(id+"F2.wireOp",EDGE,"E11"),sQuery(id+"F2.wireOp",EDGE,"E12"),sQuery(id+"F2.wireOp",EDGE,"E13"),sQuery(id+"F2.wireOp",EDGE,"E14"),sQuery(id+"F2.wireOp",EDGE,"E15"),sQuery(id+"F2.wireOp",EDGE,"E17"),sQuery(id+"F2.wireOp",EDGE,"E18"),sQuery(id+"F2.wireOp",EDGE,"E19"),sQuery(id+"F2.wireOp",EDGE,"E20.MirrorCS"),sQuery(id+"F2.wireOp",EDGE,"E21.MirrorCS"),sQuery(id+"F2.wireOp",EDGE,"E22.MirrorCS"),sQuery(id+"F2.wireOp",EDGE,"E23.MirrorCS"),sQuery(id+"F2.wireOp",EDGE,"E24.MirrorCS"),sQuery(id+"F2.wireOp",EDGE,"E25.MirrorCS")])],"isStart":false}),"instanceName":"2"})}),makeQuery(id+"F18.opPattern","COPY",FACE,{"derivedFrom":makeQuery(id+"F17.opPattern","COPY",FACE,{"derivedFrom":makeQuery(id+"F16.opExtrude","CAP_FACE",FACE,{"disambiguationData":[OSD([sQuery(id+"F15.wireOp",EDGE,"E27"),sQuery(id+"F15.wireOp",EDGE,"E28"),sQuery(id+"F15.wireOp",EDGE,"E29"),sQuery(id+"F15.wireOp",EDGE,"E30")])],"isStart":true}),"instanceName":"1"}),"instanceName":"1"})]});
            var Q12;
            Q12=makeQuery(id+"F18.boolean.opBoolean","INTERSECT",EDGE,{"derivedFrom":[makeQuery(id+"F8.opChamfer","SPLIT",FACE,{"disambiguationData":[OD(0.0)],"derivedFrom":makeQuery(id+"F7.opPattern","COPY",FACE,{"derivedFrom":makeQuery(id+"F4.opExtrude","CAP_FACE",FACE,{"disambiguationData":[OSD([sQuery(id+"F2.wireOp",EDGE,"E9"),sQuery(id+"F2.wireOp",EDGE,"E10"),sQuery(id+"F2.wireOp",EDGE,"E11"),sQuery(id+"F2.wireOp",EDGE,"E12"),sQuery(id+"F2.wireOp",EDGE,"E13"),sQuery(id+"F2.wireOp",EDGE,"E14"),sQuery(id+"F2.wireOp",EDGE,"E15"),sQuery(id+"F2.wireOp",EDGE,"E17"),sQuery(id+"F2.wireOp",EDGE,"E18"),sQuery(id+"F2.wireOp",EDGE,"E19"),sQuery(id+"F2.wireOp",EDGE,"E20.MirrorCS"),sQuery(id+"F2.wireOp",EDGE,"E21.MirrorCS"),sQuery(id+"F2.wireOp",EDGE,"E22.MirrorCS"),sQuery(id+"F2.wireOp",EDGE,"E23.MirrorCS"),sQuery(id+"F2.wireOp",EDGE,"E24.MirrorCS"),sQuery(id+"F2.wireOp",EDGE,"E25.MirrorCS")])],"isStart":false}),"instanceName":"2"})}),makeQuery(id+"F18.opPattern","COPY",FACE,{"derivedFrom":makeQuery(id+"F16.opExtrude","CAP_FACE",FACE,{"disambiguationData":[OSD([sQuery(id+"F15.wireOp",EDGE,"E27"),sQuery(id+"F15.wireOp",EDGE,"E28"),sQuery(id+"F15.wireOp",EDGE,"E29"),sQuery(id+"F15.wireOp",EDGE,"E30")])],"isStart":true}),"instanceName":"1"})]});
            var Q13;
            Q13=makeQuery(id+"F18.boolean.opBoolean","INTERSECT",EDGE,{"derivedFrom":[makeQuery(id+"F8.opChamfer","SPLIT",FACE,{"disambiguationData":[OD(0.0)],"derivedFrom":makeQuery(id+"F7.opPattern","COPY",FACE,{"derivedFrom":makeQuery(id+"F4.opExtrude","CAP_FACE",FACE,{"disambiguationData":[OSD([sQuery(id+"F2.wireOp",EDGE,"E9"),sQuery(id+"F2.wireOp",EDGE,"E10"),sQuery(id+"F2.wireOp",EDGE,"E11"),sQuery(id+"F2.wireOp",EDGE,"E12"),sQuery(id+"F2.wireOp",EDGE,"E13"),sQuery(id+"F2.wireOp",EDGE,"E14"),sQuery(id+"F2.wireOp",EDGE,"E15"),sQuery(id+"F2.wireOp",EDGE,"E17"),sQuery(id+"F2.wireOp",EDGE,"E18"),sQuery(id+"F2.wireOp",EDGE,"E19"),sQuery(id+"F2.wireOp",EDGE,"E20.MirrorCS"),sQuery(id+"F2.wireOp",EDGE,"E21.MirrorCS"),sQuery(id+"F2.wireOp",EDGE,"E22.MirrorCS"),sQuery(id+"F2.wireOp",EDGE,"E23.MirrorCS"),sQuery(id+"F2.wireOp",EDGE,"E24.MirrorCS"),sQuery(id+"F2.wireOp",EDGE,"E25.MirrorCS")])],"isStart":false}),"instanceName":"2"})}),makeQuery(id+"F18.opPattern","COPY",FACE,{"derivedFrom":makeQuery(id+"F16.opExtrude","CAP_FACE",FACE,{"disambiguationData":[OSD([sQuery(id+"F15.wireOp",EDGE,"E27"),sQuery(id+"F15.wireOp",EDGE,"E28"),sQuery(id+"F15.wireOp",EDGE,"E29"),sQuery(id+"F15.wireOp",EDGE,"E30")])],"isStart":false}),"instanceName":"1"})]});
            var Q14;
            {var subQ0=sQuery(id+"F2.wireOp",EDGE,"E10");Q14=makeQuery(id+"F18.boolean.opBoolean","INTERSECT",EDGE,{"derivedFrom":[makeQuery(id+"F10.opFillet","BLEND_FACE",FACE,{"disambiguationData":[OSD([subQ0]),TDD([makeQuery(id+"F7.opPattern","COPY",EDGE,{"derivedFrom":makeQuery(id+"F4.opExtrude","CAP_EDGE",EDGE,{"disambiguationData":[OSD([subQ0])],"isStart":false}),"instanceName":"2"})])]}),makeQuery(id+"F18.opPattern","COPY",FACE,{"derivedFrom":makeQuery(id+"F16.opExtrude","SWEPT_FACE",FACE,{"disambiguationData":[OSD([sQuery(id+"F15.wireOp",EDGE,"E30")])]}),"instanceName":"1"})]});}
            var Q15;
            {var subQ0=sQuery(id+"F2.wireOp",EDGE,"E25.MirrorCS");var subQ1=sQuery(id+"F2.wireOp",EDGE,"E19");var subQ2=sQuery(id+"F2.wireOp",EDGE,"E13");Q15=makeQuery(id+"F18.boolean.opBoolean","INTERSECT",EDGE,{"derivedFrom":[makeQuery(id+"F9.opFillet","SPLIT",FACE,{"disambiguationData":[OD(0.0)],"derivedFrom":makeQuery(id+"F8.opChamfer","BLEND_FACE",FACE,{"disambiguationData":[OSD([subQ2,subQ1,subQ0]),TDD([makeQuery(id+"F7.opPattern","COPY",EDGE,{"derivedFrom":makeQuery(id+"F4.opExtrude","CAP_EDGE",EDGE,{"disambiguationData":[OSD([subQ2,subQ1,subQ0])],"isStart":false}),"instanceName":"2"})])]})}),makeQuery(id+"F18.opPattern","COPY",FACE,{"derivedFrom":makeQuery(id+"F16.opExtrude","SWEPT_FACE",FACE,{"disambiguationData":[OSD([sQuery(id+"F15.wireOp",EDGE,"E28")])]}),"instanceName":"1"})]});}
            var Q16;
            {var subQ0=sQuery(id+"F2.wireOp",EDGE,"E10");Q16=makeQuery(id+"F18.boolean.opBoolean","INTERSECT",EDGE,{"derivedFrom":[makeQuery(id+"F10.opFillet","BLEND_FACE",FACE,{"disambiguationData":[OSD([subQ0]),TDD([makeQuery(id+"F7.opPattern","COPY",EDGE,{"derivedFrom":makeQuery(id+"F4.opExtrude","CAP_EDGE",EDGE,{"disambiguationData":[OSD([subQ0])],"isStart":false}),"instanceName":"1"})])]}),makeQuery(id+"F18.opPattern","COPY",FACE,{"derivedFrom":makeQuery(id+"F16.opExtrude","SWEPT_FACE",FACE,{"disambiguationData":[OSD([sQuery(id+"F15.wireOp",EDGE,"E30")])]}),"instanceName":"2"})]});}
            var Q17;
            {var subQ0=sQuery(id+"F2.wireOp",EDGE,"E25.MirrorCS");var subQ1=sQuery(id+"F2.wireOp",EDGE,"E19");var subQ2=sQuery(id+"F2.wireOp",EDGE,"E13");Q17=makeQuery(id+"F18.boolean.opBoolean","INTERSECT",EDGE,{"derivedFrom":[makeQuery(id+"F9.opFillet","SPLIT",FACE,{"disambiguationData":[OD(0.0)],"derivedFrom":makeQuery(id+"F8.opChamfer","BLEND_FACE",FACE,{"disambiguationData":[OSD([subQ2,subQ1,subQ0]),TDD([makeQuery(id+"F7.opPattern","COPY",EDGE,{"derivedFrom":makeQuery(id+"F4.opExtrude","CAP_EDGE",EDGE,{"disambiguationData":[OSD([subQ2,subQ1,subQ0])],"isStart":false}),"instanceName":"1"})])]})}),makeQuery(id+"F18.opPattern","COPY",FACE,{"derivedFrom":makeQuery(id+"F16.opExtrude","SWEPT_FACE",FACE,{"disambiguationData":[OSD([sQuery(id+"F15.wireOp",EDGE,"E28")])]}),"instanceName":"2"})]});}
            var Q18;
            Q18=makeQuery(id+"F18.boolean.opBoolean","INTERSECT",EDGE,{"derivedFrom":[makeQuery(id+"F8.opChamfer","SPLIT",FACE,{"disambiguationData":[OD(0.0)],"derivedFrom":makeQuery(id+"F7.opPattern","COPY",FACE,{"derivedFrom":makeQuery(id+"F4.opExtrude","CAP_FACE",FACE,{"disambiguationData":[OSD([sQuery(id+"F2.wireOp",EDGE,"E9"),sQuery(id+"F2.wireOp",EDGE,"E10"),sQuery(id+"F2.wireOp",EDGE,"E11"),sQuery(id+"F2.wireOp",EDGE,"E12"),sQuery(id+"F2.wireOp",EDGE,"E13"),sQuery(id+"F2.wireOp",EDGE,"E14"),sQuery(id+"F2.wireOp",EDGE,"E15"),sQuery(id+"F2.wireOp",EDGE,"E17"),sQuery(id+"F2.wireOp",EDGE,"E18"),sQuery(id+"F2.wireOp",EDGE,"E19"),sQuery(id+"F2.wireOp",EDGE,"E20.MirrorCS"),sQuery(id+"F2.wireOp",EDGE,"E21.MirrorCS"),sQuery(id+"F2.wireOp",EDGE,"E22.MirrorCS"),sQuery(id+"F2.wireOp",EDGE,"E23.MirrorCS"),sQuery(id+"F2.wireOp",EDGE,"E24.MirrorCS"),sQuery(id+"F2.wireOp",EDGE,"E25.MirrorCS")])],"isStart":false}),"instanceName":"1"})}),makeQuery(id+"F18.opPattern","COPY",FACE,{"derivedFrom":makeQuery(id+"F16.opExtrude","CAP_FACE",FACE,{"disambiguationData":[OSD([sQuery(id+"F15.wireOp",EDGE,"E27"),sQuery(id+"F15.wireOp",EDGE,"E28"),sQuery(id+"F15.wireOp",EDGE,"E29"),sQuery(id+"F15.wireOp",EDGE,"E30")])],"isStart":true}),"instanceName":"2"})]});
            var Q19;
            Q19=makeQuery(id+"F18.boolean.opBoolean","INTERSECT",EDGE,{"derivedFrom":[makeQuery(id+"F8.opChamfer","SPLIT",FACE,{"disambiguationData":[OD(0.0)],"derivedFrom":makeQuery(id+"F7.opPattern","COPY",FACE,{"derivedFrom":makeQuery(id+"F4.opExtrude","CAP_FACE",FACE,{"disambiguationData":[OSD([sQuery(id+"F2.wireOp",EDGE,"E9"),sQuery(id+"F2.wireOp",EDGE,"E10"),sQuery(id+"F2.wireOp",EDGE,"E11"),sQuery(id+"F2.wireOp",EDGE,"E12"),sQuery(id+"F2.wireOp",EDGE,"E13"),sQuery(id+"F2.wireOp",EDGE,"E14"),sQuery(id+"F2.wireOp",EDGE,"E15"),sQuery(id+"F2.wireOp",EDGE,"E17"),sQuery(id+"F2.wireOp",EDGE,"E18"),sQuery(id+"F2.wireOp",EDGE,"E19"),sQuery(id+"F2.wireOp",EDGE,"E20.MirrorCS"),sQuery(id+"F2.wireOp",EDGE,"E21.MirrorCS"),sQuery(id+"F2.wireOp",EDGE,"E22.MirrorCS"),sQuery(id+"F2.wireOp",EDGE,"E23.MirrorCS"),sQuery(id+"F2.wireOp",EDGE,"E24.MirrorCS"),sQuery(id+"F2.wireOp",EDGE,"E25.MirrorCS")])],"isStart":false}),"instanceName":"1"})}),makeQuery(id+"F18.opPattern","COPY",FACE,{"derivedFrom":makeQuery(id+"F16.opExtrude","CAP_FACE",FACE,{"disambiguationData":[OSD([sQuery(id+"F15.wireOp",EDGE,"E27"),sQuery(id+"F15.wireOp",EDGE,"E28"),sQuery(id+"F15.wireOp",EDGE,"E29"),sQuery(id+"F15.wireOp",EDGE,"E30")])],"isStart":false}),"instanceName":"2"})]});
            var Q20;
            Q20=makeQuery(id+"F18.boolean.opBoolean","INTERSECT",EDGE,{"derivedFrom":[makeQuery(id+"F8.opChamfer","SPLIT",FACE,{"disambiguationData":[OD(0.0)],"derivedFrom":makeQuery(id+"F7.opPattern","COPY",FACE,{"derivedFrom":makeQuery(id+"F4.opExtrude","CAP_FACE",FACE,{"disambiguationData":[OSD([sQuery(id+"F2.wireOp",EDGE,"E9"),sQuery(id+"F2.wireOp",EDGE,"E10"),sQuery(id+"F2.wireOp",EDGE,"E11"),sQuery(id+"F2.wireOp",EDGE,"E12"),sQuery(id+"F2.wireOp",EDGE,"E13"),sQuery(id+"F2.wireOp",EDGE,"E14"),sQuery(id+"F2.wireOp",EDGE,"E15"),sQuery(id+"F2.wireOp",EDGE,"E17"),sQuery(id+"F2.wireOp",EDGE,"E18"),sQuery(id+"F2.wireOp",EDGE,"E19"),sQuery(id+"F2.wireOp",EDGE,"E20.MirrorCS"),sQuery(id+"F2.wireOp",EDGE,"E21.MirrorCS"),sQuery(id+"F2.wireOp",EDGE,"E22.MirrorCS"),sQuery(id+"F2.wireOp",EDGE,"E23.MirrorCS"),sQuery(id+"F2.wireOp",EDGE,"E24.MirrorCS"),sQuery(id+"F2.wireOp",EDGE,"E25.MirrorCS")])],"isStart":false}),"instanceName":"1"})}),makeQuery(id+"F18.opPattern","COPY",FACE,{"derivedFrom":makeQuery(id+"F17.opPattern","COPY",FACE,{"derivedFrom":makeQuery(id+"F16.opExtrude","CAP_FACE",FACE,{"disambiguationData":[OSD([sQuery(id+"F15.wireOp",EDGE,"E27"),sQuery(id+"F15.wireOp",EDGE,"E28"),sQuery(id+"F15.wireOp",EDGE,"E29"),sQuery(id+"F15.wireOp",EDGE,"E30")])],"isStart":true}),"instanceName":"1"}),"instanceName":"2"})]});
            var Q21;
            Q21=makeQuery(id+"F18.boolean.opBoolean","INTERSECT",EDGE,{"derivedFrom":[makeQuery(id+"F8.opChamfer","SPLIT",FACE,{"disambiguationData":[OD(0.0)],"derivedFrom":makeQuery(id+"F7.opPattern","COPY",FACE,{"derivedFrom":makeQuery(id+"F4.opExtrude","CAP_FACE",FACE,{"disambiguationData":[OSD([sQuery(id+"F2.wireOp",EDGE,"E9"),sQuery(id+"F2.wireOp",EDGE,"E10"),sQuery(id+"F2.wireOp",EDGE,"E11"),sQuery(id+"F2.wireOp",EDGE,"E12"),sQuery(id+"F2.wireOp",EDGE,"E13"),sQuery(id+"F2.wireOp",EDGE,"E14"),sQuery(id+"F2.wireOp",EDGE,"E15"),sQuery(id+"F2.wireOp",EDGE,"E17"),sQuery(id+"F2.wireOp",EDGE,"E18"),sQuery(id+"F2.wireOp",EDGE,"E19"),sQuery(id+"F2.wireOp",EDGE,"E20.MirrorCS"),sQuery(id+"F2.wireOp",EDGE,"E21.MirrorCS"),sQuery(id+"F2.wireOp",EDGE,"E22.MirrorCS"),sQuery(id+"F2.wireOp",EDGE,"E23.MirrorCS"),sQuery(id+"F2.wireOp",EDGE,"E24.MirrorCS"),sQuery(id+"F2.wireOp",EDGE,"E25.MirrorCS")])],"isStart":false}),"instanceName":"1"})}),makeQuery(id+"F18.opPattern","COPY",FACE,{"derivedFrom":makeQuery(id+"F17.opPattern","COPY",FACE,{"derivedFrom":makeQuery(id+"F16.opExtrude","CAP_FACE",FACE,{"disambiguationData":[OSD([sQuery(id+"F15.wireOp",EDGE,"E27"),sQuery(id+"F15.wireOp",EDGE,"E28"),sQuery(id+"F15.wireOp",EDGE,"E29"),sQuery(id+"F15.wireOp",EDGE,"E30")])],"isStart":false}),"instanceName":"1"}),"instanceName":"2"})]});
            var Q22;
            {var subQ0=sQuery(id+"F2.wireOp",EDGE,"E10");Q22=makeQuery(id+"F18.boolean.opBoolean","INTERSECT",EDGE,{"derivedFrom":[makeQuery(id+"F10.opFillet","BLEND_FACE",FACE,{"disambiguationData":[OSD([subQ0]),TDD([makeQuery(id+"F7.opPattern","COPY",EDGE,{"derivedFrom":makeQuery(id+"F4.opExtrude","CAP_EDGE",EDGE,{"disambiguationData":[OSD([subQ0])],"isStart":false}),"instanceName":"1"})])]}),makeQuery(id+"F18.opPattern","COPY",FACE,{"derivedFrom":makeQuery(id+"F17.opPattern","COPY",FACE,{"derivedFrom":makeQuery(id+"F16.opExtrude","SWEPT_FACE",FACE,{"disambiguationData":[OSD([sQuery(id+"F15.wireOp",EDGE,"E30")])]}),"instanceName":"1"}),"instanceName":"2"})]});}
            var Q23;
            {var subQ0=sQuery(id+"F2.wireOp",EDGE,"E25.MirrorCS");var subQ1=sQuery(id+"F2.wireOp",EDGE,"E19");var subQ2=sQuery(id+"F2.wireOp",EDGE,"E13");Q23=makeQuery(id+"F18.boolean.opBoolean","INTERSECT",EDGE,{"derivedFrom":[makeQuery(id+"F9.opFillet","SPLIT",FACE,{"disambiguationData":[OD(0.0)],"derivedFrom":makeQuery(id+"F8.opChamfer","BLEND_FACE",FACE,{"disambiguationData":[OSD([subQ2,subQ1,subQ0]),TDD([makeQuery(id+"F7.opPattern","COPY",EDGE,{"derivedFrom":makeQuery(id+"F4.opExtrude","CAP_EDGE",EDGE,{"disambiguationData":[OSD([subQ2,subQ1,subQ0])],"isStart":false}),"instanceName":"1"})])]})}),makeQuery(id+"F18.opPattern","COPY",FACE,{"derivedFrom":makeQuery(id+"F17.opPattern","COPY",FACE,{"derivedFrom":makeQuery(id+"F16.opExtrude","SWEPT_FACE",FACE,{"disambiguationData":[OSD([sQuery(id+"F15.wireOp",EDGE,"E28")])]}),"instanceName":"1"}),"instanceName":"2"})]});}
            fillet(context, id + "F19", {"entities" : qUnion([Q0, Q1, Q2, Q3, Q4, Q5, Q6, Q7, Q8, Q9, Q10, Q11, Q12, Q13, Q14, Q15, Q16, Q17, Q18, Q19, Q20, Q21, Q22, Q23]), "radius" : 0.3 * mm, "tangentPropagation" : true, "allowEdgeOverflow" : false});
        }
    });
